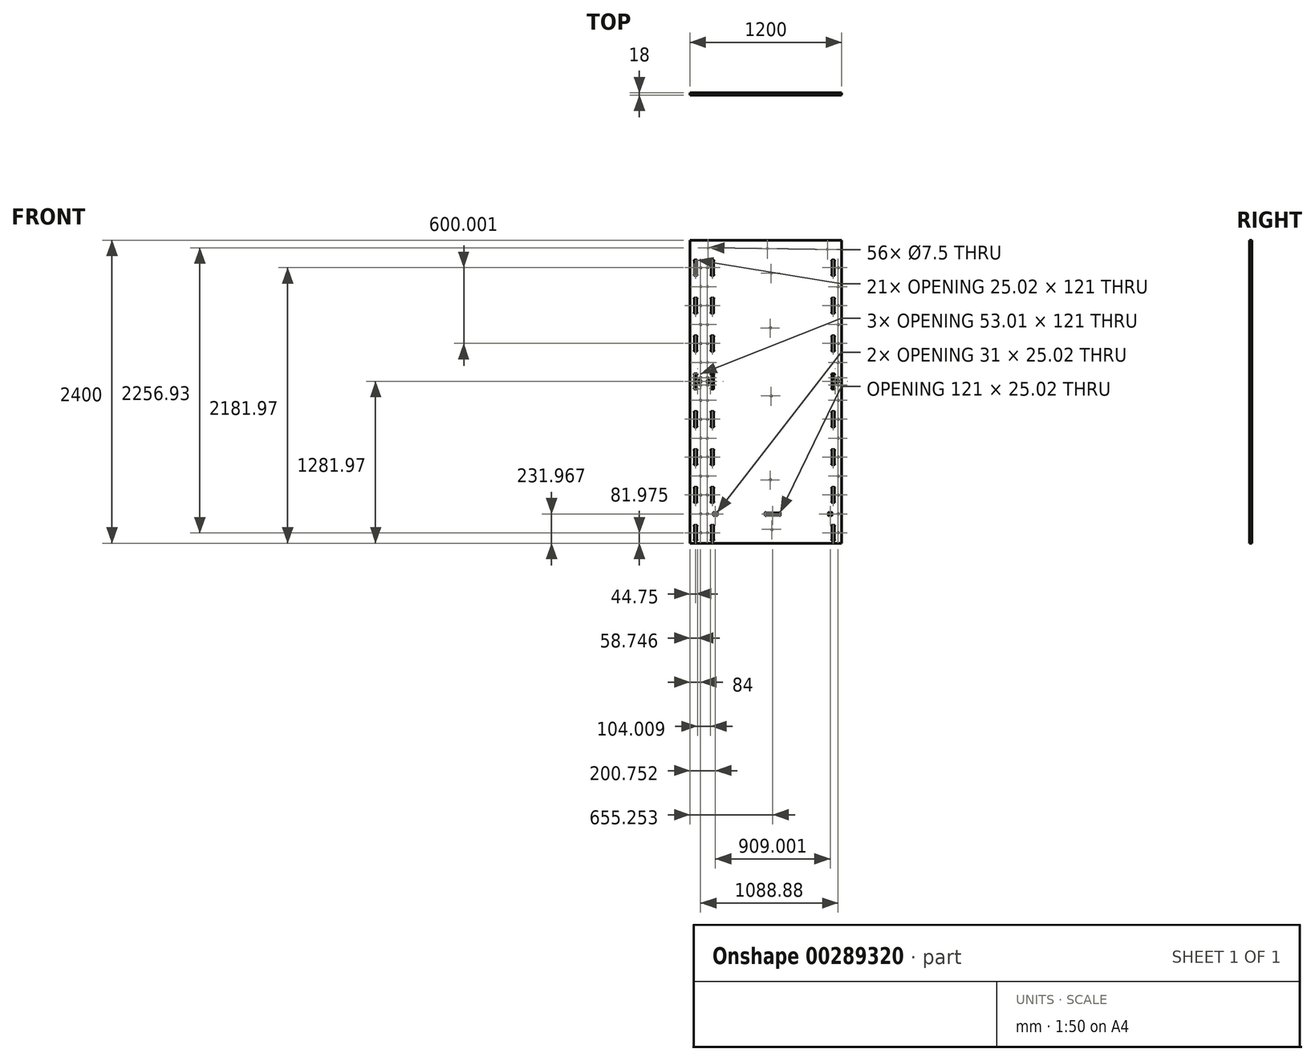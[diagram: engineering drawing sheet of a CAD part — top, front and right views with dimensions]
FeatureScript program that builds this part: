
annotation { "Feature Type Name" : "Feature", "Feature Type Description" : "" }
export const myFeature = defineFeature(function(context is Context, id is Id, definition is map)
    precondition{}
    {
        {
            var Q0;
            Q0=qCreatedBy(makeId("Front.planeOp"),FACE);
            var sketch = newSketch(context, id + "F0", { "sketchPlane" : qUnion([Q0])});
            skLineSegment(sketch, "E0", {"start": v(-600, -1200) * mm, "end": v(600, -1200) * mm});
            skLineSegment(sketch, "E1", {"start": v(600, -1200) * mm, "end": v(600, 1200) * mm});
            skLineSegment(sketch, "E2", {"start": v(600, 1200) * mm, "end": v(-600, 1200) * mm});
            skLineSegment(sketch, "E3", {"start": v(-600, 1200) * mm, "end": v(-600, -1200) * mm});
            skLineSegment(sketch, "E4", {"start": v(-600, 1063.95) * mm, "end": v(-5, 1063.95) * mm});
            skLineSegment(sketch, "E5", {"start": v(-5, 1063.95) * mm, "end": v(-5, 1053.8) * mm});
            skArc(sketch, "E6", {"start": v(-5, 1053.8) * mm, "mid": v(-1.86, 1050.55) * mm, "end": v(1.52, 1053.56) * mm});
            skLineSegment(sketch, "E7", {"start": v(1.52, 1053.56) * mm, "end": v(108.98, 1053.56) * mm});
            skArc(sketch, "E8", {"start": v(108.98, 1053.56) * mm, "mid": v(112.36, 1050.54) * mm, "end": v(115.5, 1053.8) * mm});
            skLineSegment(sketch, "E9", {"start": v(115.5, 1053.8) * mm, "end": v(115.5, 1063.95) * mm});
            skLineSegment(sketch, "E10", {"start": v(115.5, 1063.95) * mm, "end": v(599.5, 1063.95) * mm});
            skLineSegment(sketch, "E11", {"start": v(599.5, 1063.95) * mm, "end": v(599.5, -1200) * mm});
            skArc(sketch, "E12", {"start": v(543, -278.53) * mm, "mid": v(546.26, -275.4) * mm, "end": v(543.25, -272.02) * mm});
            skLineSegment(sketch, "E13", {"start": v(543.25, -272.02) * mm, "end": v(543.25, -164.04) * mm});
            skArc(sketch, "E14", {"start": v(543.25, -164.04) * mm, "mid": v(546.26, -160.67) * mm, "end": v(543, -157.53) * mm});
            skLineSegment(sketch, "E15", {"start": v(543, -157.53) * mm, "end": v(524.5, -157.53) * mm});
            skArc(sketch, "E16", {"start": v(524.5, -157.53) * mm, "mid": v(521.24, -160.67) * mm, "end": v(524.25, -164.04) * mm});
            skLineSegment(sketch, "E17", {"start": v(524.25, -164.04) * mm, "end": v(524.25, -272.02) * mm});
            skArc(sketch, "E18", {"start": v(524.25, -272.02) * mm, "mid": v(521.24, -275.4) * mm, "end": v(524.5, -278.53) * mm});
            skLineSegment(sketch, "E19", {"start": v(524.5, -278.53) * mm, "end": v(543, -278.53) * mm});
            skArc(sketch, "E20", {"start": v(524.25, 27.98) * mm, "mid": v(521.24, 24.6) * mm, "end": v(524.5, 21.47) * mm});
            skLineSegment(sketch, "E21", {"start": v(524.5, 21.47) * mm, "end": v(543, 21.47) * mm});
            skArc(sketch, "E22", {"start": v(543, 21.47) * mm, "mid": v(546.26, 24.6) * mm, "end": v(543.25, 27.98) * mm});
            skLineSegment(sketch, "E23", {"start": v(543.25, 27.98) * mm, "end": v(543.25, 72.47) * mm});
            skLineSegment(sketch, "E24", {"start": v(543.25, 72.47) * mm, "end": v(567.74, 72.47) * mm});
            skArc(sketch, "E25", {"start": v(567.74, 72.47) * mm, "mid": v(571.12, 69.46) * mm, "end": v(574.25, 72.72) * mm});
            skLineSegment(sketch, "E26", {"start": v(574.25, 72.72) * mm, "end": v(574.25, 91.22) * mm});
            skArc(sketch, "E27", {"start": v(574.25, 91.22) * mm, "mid": v(571.12, 94.48) * mm, "end": v(567.74, 91.47) * mm});
            skLineSegment(sketch, "E28", {"start": v(567.74, 91.47) * mm, "end": v(543.25, 91.47) * mm});
            skLineSegment(sketch, "E29", {"start": v(543.25, 91.47) * mm, "end": v(543.25, 135.96) * mm});
            skArc(sketch, "E30", {"start": v(543.25, 135.96) * mm, "mid": v(546.26, 139.33) * mm, "end": v(543, 142.47) * mm});
            skLineSegment(sketch, "E31", {"start": v(543, 142.47) * mm, "end": v(524.5, 142.47) * mm});
            skArc(sketch, "E32", {"start": v(524.5, 142.47) * mm, "mid": v(521.24, 139.33) * mm, "end": v(524.25, 135.96) * mm});
            skLineSegment(sketch, "E33", {"start": v(524.25, 135.96) * mm, "end": v(524.25, 27.98) * mm});
            skArc(sketch, "E34", {"start": v(524.25, 327.98) * mm, "mid": v(521.24, 324.6) * mm, "end": v(524.5, 321.47) * mm});
            skLineSegment(sketch, "E35", {"start": v(524.5, 321.47) * mm, "end": v(543, 321.47) * mm});
            skArc(sketch, "E36", {"start": v(543, 321.47) * mm, "mid": v(546.26, 324.6) * mm, "end": v(543.25, 327.98) * mm});
            skLineSegment(sketch, "E37", {"start": v(543.25, 327.98) * mm, "end": v(543.25, 435.96) * mm});
            skArc(sketch, "E38", {"start": v(543.25, 435.96) * mm, "mid": v(546.26, 439.33) * mm, "end": v(543, 442.47) * mm});
            skLineSegment(sketch, "E39", {"start": v(543, 442.47) * mm, "end": v(524.5, 442.47) * mm});
            skArc(sketch, "E40", {"start": v(524.5, 442.47) * mm, "mid": v(521.24, 439.33) * mm, "end": v(524.25, 435.96) * mm});
            skLineSegment(sketch, "E41", {"start": v(524.25, 435.96) * mm, "end": v(524.25, 327.98) * mm});
            skArc(sketch, "E42", {"start": v(-414, 621.47) * mm, "mid": v(-410.74, 624.6) * mm, "end": v(-413.75, 627.99) * mm});
            skLineSegment(sketch, "E43", {"start": v(-413.75, 627.99) * mm, "end": v(-413.75, 735.96) * mm});
            skArc(sketch, "E44", {"start": v(-413.75, 735.96) * mm, "mid": v(-410.74, 739.34) * mm, "end": v(-414, 742.47) * mm});
            skLineSegment(sketch, "E45", {"start": v(-414, 742.47) * mm, "end": v(-432.5, 742.47) * mm});
            skArc(sketch, "E46", {"start": v(-432.5, 742.47) * mm, "mid": v(-435.76, 739.34) * mm, "end": v(-432.75, 735.96) * mm});
            skLineSegment(sketch, "E47", {"start": v(-432.75, 735.96) * mm, "end": v(-432.75, 627.99) * mm});
            skArc(sketch, "E48", {"start": v(-432.75, 627.99) * mm, "mid": v(-435.76, 624.6) * mm, "end": v(-432.5, 621.47) * mm});
            skLineSegment(sketch, "E49", {"start": v(-432.5, 621.47) * mm, "end": v(-414, 621.47) * mm});
            skArc(sketch, "E50", {"start": v(-432.5, 442.47) * mm, "mid": v(-435.76, 439.34) * mm, "end": v(-432.75, 435.96) * mm});
            skLineSegment(sketch, "E51", {"start": v(-432.75, 435.96) * mm, "end": v(-432.75, 327.99) * mm});
            skArc(sketch, "E52", {"start": v(-432.75, 327.99) * mm, "mid": v(-435.76, 324.6) * mm, "end": v(-432.5, 321.47) * mm});
            skLineSegment(sketch, "E53", {"start": v(-432.5, 321.47) * mm, "end": v(-414, 321.47) * mm});
            skArc(sketch, "E54", {"start": v(-414, 321.47) * mm, "mid": v(-410.74, 324.6) * mm, "end": v(-413.75, 327.99) * mm});
            skLineSegment(sketch, "E55", {"start": v(-413.75, 327.99) * mm, "end": v(-413.75, 435.96) * mm});
            skArc(sketch, "E56", {"start": v(-413.75, 435.96) * mm, "mid": v(-410.74, 439.34) * mm, "end": v(-414, 442.47) * mm});
            skLineSegment(sketch, "E57", {"start": v(-414, 442.47) * mm, "end": v(-432.5, 442.47) * mm});
            skArc(sketch, "E58", {"start": v(-432.5, 142.47) * mm, "mid": v(-435.76, 139.33) * mm, "end": v(-432.75, 135.96) * mm});
            skLineSegment(sketch, "E59", {"start": v(-432.75, 135.96) * mm, "end": v(-432.75, 91.47) * mm});
            skLineSegment(sketch, "E60", {"start": v(-432.75, 91.47) * mm, "end": v(-457.24, 91.47) * mm});
            skArc(sketch, "E61", {"start": v(-457.24, 91.47) * mm, "mid": v(-460.61, 94.47) * mm, "end": v(-463.75, 91.22) * mm});
            skLineSegment(sketch, "E62", {"start": v(-463.75, 91.22) * mm, "end": v(-463.75, 72.72) * mm});
            skArc(sketch, "E63", {"start": v(-463.75, 72.72) * mm, "mid": v(-460.61, 69.46) * mm, "end": v(-457.24, 72.47) * mm});
            skLineSegment(sketch, "E64", {"start": v(-457.24, 72.47) * mm, "end": v(-432.75, 72.47) * mm});
            skLineSegment(sketch, "E65", {"start": v(-432.75, 72.47) * mm, "end": v(-432.75, 27.98) * mm});
            skArc(sketch, "E66", {"start": v(-432.75, 27.98) * mm, "mid": v(-435.76, 24.6) * mm, "end": v(-432.5, 21.47) * mm});
            skLineSegment(sketch, "E67", {"start": v(-432.5, 21.47) * mm, "end": v(-414, 21.47) * mm});
            skArc(sketch, "E68", {"start": v(-414, 21.47) * mm, "mid": v(-410.74, 24.6) * mm, "end": v(-413.75, 27.98) * mm});
            skLineSegment(sketch, "E69", {"start": v(-413.75, 27.98) * mm, "end": v(-413.75, 135.96) * mm});
            skArc(sketch, "E70", {"start": v(-413.75, 135.96) * mm, "mid": v(-410.74, 139.33) * mm, "end": v(-414, 142.47) * mm});
            skLineSegment(sketch, "E71", {"start": v(-414, 142.47) * mm, "end": v(-432.5, 142.47) * mm});
            skArc(sketch, "E72", {"start": v(-432.5, -157.53) * mm, "mid": v(-435.76, -160.66) * mm, "end": v(-432.75, -164.04) * mm});
            skLineSegment(sketch, "E73", {"start": v(-432.75, -164.04) * mm, "end": v(-432.75, -272.02) * mm});
            skArc(sketch, "E74", {"start": v(-432.75, -272.02) * mm, "mid": v(-435.76, -275.4) * mm, "end": v(-432.5, -278.53) * mm});
            skLineSegment(sketch, "E75", {"start": v(-432.5, -278.53) * mm, "end": v(-414, -278.53) * mm});
            skArc(sketch, "E76", {"start": v(-414, -278.53) * mm, "mid": v(-410.74, -275.4) * mm, "end": v(-413.75, -272.02) * mm});
            skLineSegment(sketch, "E77", {"start": v(-413.75, -272.02) * mm, "end": v(-413.75, -164.04) * mm});
            skArc(sketch, "E78", {"start": v(-413.75, -164.04) * mm, "mid": v(-410.74, -160.66) * mm, "end": v(-414, -157.53) * mm});
            skLineSegment(sketch, "E79", {"start": v(-414, -157.53) * mm, "end": v(-432.5, -157.53) * mm});
            skArc(sketch, "E80", {"start": v(-432.5, -457.53) * mm, "mid": v(-435.76, -460.66) * mm, "end": v(-432.75, -464.04) * mm});
            skLineSegment(sketch, "E81", {"start": v(-432.75, -464.04) * mm, "end": v(-432.75, -572.02) * mm});
            skArc(sketch, "E82", {"start": v(-432.75, -572.02) * mm, "mid": v(-435.76, -575.4) * mm, "end": v(-432.5, -578.53) * mm});
            skLineSegment(sketch, "E83", {"start": v(-432.5, -578.53) * mm, "end": v(-414, -578.53) * mm});
            skArc(sketch, "E84", {"start": v(-414, -578.53) * mm, "mid": v(-410.74, -575.4) * mm, "end": v(-413.75, -572.02) * mm});
            skLineSegment(sketch, "E85", {"start": v(-413.75, -572.02) * mm, "end": v(-413.75, -464.04) * mm});
            skArc(sketch, "E86", {"start": v(-413.75, -464.04) * mm, "mid": v(-410.74, -460.66) * mm, "end": v(-414, -457.53) * mm});
            skLineSegment(sketch, "E87", {"start": v(-414, -457.53) * mm, "end": v(-432.5, -457.53) * mm});
            skArc(sketch, "E88", {"start": v(-432.5, -757.53) * mm, "mid": v(-435.76, -760.66) * mm, "end": v(-432.75, -764.04) * mm});
            skLineSegment(sketch, "E89", {"start": v(-432.75, -764.04) * mm, "end": v(-432.75, -872.02) * mm});
            skArc(sketch, "E90", {"start": v(-432.75, -872.02) * mm, "mid": v(-435.76, -875.4) * mm, "end": v(-432.5, -878.53) * mm});
            skLineSegment(sketch, "E91", {"start": v(-432.5, -878.53) * mm, "end": v(-414, -878.53) * mm});
            skArc(sketch, "E92", {"start": v(-414, -878.53) * mm, "mid": v(-410.74, -875.4) * mm, "end": v(-413.75, -872.02) * mm});
            skLineSegment(sketch, "E93", {"start": v(-413.75, -872.02) * mm, "end": v(-413.75, -764.04) * mm});
            skArc(sketch, "E94", {"start": v(-413.75, -764.04) * mm, "mid": v(-410.74, -760.66) * mm, "end": v(-414, -757.53) * mm});
            skLineSegment(sketch, "E95", {"start": v(-414, -757.53) * mm, "end": v(-432.5, -757.53) * mm});
            skArc(sketch, "E96", {"start": v(-545.75, -764.04) * mm, "mid": v(-542.74, -760.66) * mm, "end": v(-546, -757.53) * mm});
            skLineSegment(sketch, "E97", {"start": v(-546, -757.53) * mm, "end": v(-564.5, -757.53) * mm});
            skArc(sketch, "E98", {"start": v(-564.5, -757.53) * mm, "mid": v(-567.76, -760.66) * mm, "end": v(-564.75, -764.04) * mm});
            skLineSegment(sketch, "E99", {"start": v(-564.75, -764.04) * mm, "end": v(-564.75, -872.02) * mm});
            skArc(sketch, "E100", {"start": v(-564.75, -872.02) * mm, "mid": v(-567.76, -875.4) * mm, "end": v(-564.5, -878.53) * mm});
            skLineSegment(sketch, "E101", {"start": v(-564.5, -878.53) * mm, "end": v(-546, -878.53) * mm});
            skArc(sketch, "E102", {"start": v(-546, -878.53) * mm, "mid": v(-542.74, -875.4) * mm, "end": v(-545.75, -872.02) * mm});
            skLineSegment(sketch, "E103", {"start": v(-545.75, -872.02) * mm, "end": v(-545.75, -764.04) * mm});
            skArc(sketch, "E104", {"start": v(-408.24, -958.53) * mm, "mid": v(-411.61, -955.52) * mm, "end": v(-414.75, -958.78) * mm});
            skLineSegment(sketch, "E105", {"start": v(-414.75, -958.78) * mm, "end": v(-414.75, -977.28) * mm});
            skArc(sketch, "E106", {"start": v(-414.75, -977.28) * mm, "mid": v(-411.61, -980.54) * mm, "end": v(-408.24, -977.53) * mm});
            skLineSegment(sketch, "E107", {"start": v(-408.24, -977.53) * mm, "end": v(-390.26, -977.53) * mm});
            skArc(sketch, "E108", {"start": v(-390.26, -977.53) * mm, "mid": v(-386.88, -980.54) * mm, "end": v(-383.75, -977.28) * mm});
            skLineSegment(sketch, "E109", {"start": v(-383.75, -977.28) * mm, "end": v(-383.75, -958.78) * mm});
            skArc(sketch, "E110", {"start": v(-383.75, -958.78) * mm, "mid": v(-386.88, -955.52) * mm, "end": v(-390.26, -958.53) * mm});
            skLineSegment(sketch, "E111", {"start": v(-390.26, -958.53) * mm, "end": v(-408.24, -958.53) * mm});
            skArc(sketch, "E112", {"start": v(-5.25, -977.28) * mm, "mid": v(-2.11, -980.54) * mm, "end": v(1.26, -977.53) * mm});
            skLineSegment(sketch, "E113", {"start": v(1.26, -977.53) * mm, "end": v(109.24, -977.53) * mm});
            skArc(sketch, "E114", {"start": v(109.24, -977.53) * mm, "mid": v(112.62, -980.54) * mm, "end": v(115.75, -977.28) * mm});
            skLineSegment(sketch, "E115", {"start": v(115.75, -977.28) * mm, "end": v(115.75, -958.78) * mm});
            skArc(sketch, "E116", {"start": v(115.75, -958.78) * mm, "mid": v(112.62, -955.52) * mm, "end": v(109.24, -958.53) * mm});
            skLineSegment(sketch, "E117", {"start": v(109.24, -958.53) * mm, "end": v(1.26, -958.53) * mm});
            skArc(sketch, "E118", {"start": v(1.26, -958.53) * mm, "mid": v(-2.11, -955.52) * mm, "end": v(-5.25, -958.78) * mm});
            skLineSegment(sketch, "E119", {"start": v(-5.25, -958.78) * mm, "end": v(-5.25, -977.28) * mm});
            skArc(sketch, "E120", {"start": v(494.25, -977.28) * mm, "mid": v(497.39, -980.54) * mm, "end": v(500.76, -977.53) * mm});
            skLineSegment(sketch, "E121", {"start": v(500.76, -977.53) * mm, "end": v(518.74, -977.53) * mm});
            skArc(sketch, "E122", {"start": v(518.74, -977.53) * mm, "mid": v(522.12, -980.54) * mm, "end": v(525.25, -977.28) * mm});
            skLineSegment(sketch, "E123", {"start": v(525.25, -977.28) * mm, "end": v(525.25, -958.78) * mm});
            skArc(sketch, "E124", {"start": v(525.25, -958.78) * mm, "mid": v(522.12, -955.52) * mm, "end": v(518.74, -958.53) * mm});
            skLineSegment(sketch, "E125", {"start": v(518.74, -958.53) * mm, "end": v(500.76, -958.53) * mm});
            skArc(sketch, "E126", {"start": v(500.76, -958.53) * mm, "mid": v(497.39, -955.52) * mm, "end": v(494.25, -958.78) * mm});
            skLineSegment(sketch, "E127", {"start": v(494.25, -958.78) * mm, "end": v(494.25, -977.28) * mm});
            skArc(sketch, "E128", {"start": v(543, -878.53) * mm, "mid": v(546.26, -875.4) * mm, "end": v(543.25, -872.02) * mm});
            skLineSegment(sketch, "E129", {"start": v(543.25, -872.02) * mm, "end": v(543.25, -764.04) * mm});
            skArc(sketch, "E130", {"start": v(543.25, -764.04) * mm, "mid": v(546.26, -760.67) * mm, "end": v(543, -757.53) * mm});
            skLineSegment(sketch, "E131", {"start": v(543, -757.53) * mm, "end": v(524.5, -757.53) * mm});
            skArc(sketch, "E132", {"start": v(524.5, -757.53) * mm, "mid": v(521.24, -760.67) * mm, "end": v(524.25, -764.04) * mm});
            skLineSegment(sketch, "E133", {"start": v(524.25, -764.04) * mm, "end": v(524.25, -872.02) * mm});
            skArc(sketch, "E134", {"start": v(524.25, -872.02) * mm, "mid": v(521.24, -875.4) * mm, "end": v(524.5, -878.53) * mm});
            skLineSegment(sketch, "E135", {"start": v(524.5, -878.53) * mm, "end": v(543, -878.53) * mm});
            skArc(sketch, "E136", {"start": v(524.25, -572.02) * mm, "mid": v(521.24, -575.4) * mm, "end": v(524.5, -578.53) * mm});
            skLineSegment(sketch, "E137", {"start": v(524.5, -578.53) * mm, "end": v(543, -578.53) * mm});
            skArc(sketch, "E138", {"start": v(543, -578.53) * mm, "mid": v(546.26, -575.4) * mm, "end": v(543.25, -572.02) * mm});
            skLineSegment(sketch, "E139", {"start": v(543.25, -572.02) * mm, "end": v(543.25, -464.04) * mm});
            skArc(sketch, "E140", {"start": v(543.25, -464.04) * mm, "mid": v(546.26, -460.67) * mm, "end": v(543, -457.53) * mm});
            skLineSegment(sketch, "E141", {"start": v(543, -457.53) * mm, "end": v(524.5, -457.53) * mm});
            skArc(sketch, "E142", {"start": v(524.5, -457.53) * mm, "mid": v(521.24, -460.67) * mm, "end": v(524.25, -464.04) * mm});
            skLineSegment(sketch, "E143", {"start": v(524.25, -464.04) * mm, "end": v(524.25, -572.02) * mm});
            skArc(sketch, "E144", {"start": v(524.5, -1057.53) * mm, "mid": v(521.24, -1060.67) * mm, "end": v(524.25, -1064.04) * mm});
            skLineSegment(sketch, "E145", {"start": v(524.25, -1064.04) * mm, "end": v(524.25, -1172.02) * mm});
            skArc(sketch, "E146", {"start": v(524.25, -1172.02) * mm, "mid": v(521.24, -1175.4) * mm, "end": v(524.5, -1178.53) * mm});
            skLineSegment(sketch, "E147", {"start": v(524.5, -1178.53) * mm, "end": v(543, -1178.53) * mm});
            skArc(sketch, "E148", {"start": v(543, -1178.53) * mm, "mid": v(546.26, -1175.4) * mm, "end": v(543.25, -1172.02) * mm});
            skLineSegment(sketch, "E149", {"start": v(543.25, -1172.02) * mm, "end": v(543.25, -1064.04) * mm});
            skArc(sketch, "E150", {"start": v(543.25, -1064.04) * mm, "mid": v(546.26, -1060.67) * mm, "end": v(543, -1057.53) * mm});
            skLineSegment(sketch, "E151", {"start": v(543, -1057.53) * mm, "end": v(524.5, -1057.53) * mm});
            skArc(sketch, "E152", {"start": v(-545.75, -1064.05) * mm, "mid": v(-542.74, -1060.67) * mm, "end": v(-546, -1057.54) * mm});
            skLineSegment(sketch, "E153", {"start": v(-546, -1057.54) * mm, "end": v(-564.5, -1057.54) * mm});
            skArc(sketch, "E154", {"start": v(-564.5, -1057.54) * mm, "mid": v(-567.76, -1060.67) * mm, "end": v(-564.75, -1064.05) * mm});
            skLineSegment(sketch, "E155", {"start": v(-564.75, -1064.05) * mm, "end": v(-564.75, -1172.03) * mm});
            skArc(sketch, "E156", {"start": v(-564.75, -1172.03) * mm, "mid": v(-567.76, -1175.4) * mm, "end": v(-564.5, -1178.54) * mm});
            skLineSegment(sketch, "E157", {"start": v(-564.5, -1178.54) * mm, "end": v(-546, -1178.54) * mm});
            skArc(sketch, "E158", {"start": v(-546, -1178.54) * mm, "mid": v(-542.74, -1175.4) * mm, "end": v(-545.75, -1172.03) * mm});
            skLineSegment(sketch, "E159", {"start": v(-545.75, -1172.03) * mm, "end": v(-545.75, -1064.05) * mm});
            skLineSegment(sketch, "E160", {"start": v(-432.75, -1064.05) * mm, "end": v(-432.75, -1172.03) * mm});
            skArc(sketch, "E161", {"start": v(-432.75, -1172.03) * mm, "mid": v(-435.76, -1175.4) * mm, "end": v(-432.5, -1178.54) * mm});
            skLineSegment(sketch, "E162", {"start": v(-432.5, -1178.54) * mm, "end": v(-414, -1178.54) * mm});
            skArc(sketch, "E163", {"start": v(-414, -1178.54) * mm, "mid": v(-410.74, -1175.4) * mm, "end": v(-413.75, -1172.03) * mm});
            skLineSegment(sketch, "E164", {"start": v(-413.75, -1172.03) * mm, "end": v(-413.75, -1064.05) * mm});
            skArc(sketch, "E165", {"start": v(-413.75, -1064.05) * mm, "mid": v(-410.74, -1060.67) * mm, "end": v(-414, -1057.54) * mm});
            skLineSegment(sketch, "E166", {"start": v(-414, -1057.54) * mm, "end": v(-432.5, -1057.54) * mm});
            skArc(sketch, "E167", {"start": v(-432.5, -1057.54) * mm, "mid": v(-435.76, -1060.67) * mm, "end": v(-432.75, -1064.05) * mm});
            skArc(sketch, "E168", {"start": v(-545.75, -464.04) * mm, "mid": v(-542.74, -460.66) * mm, "end": v(-546, -457.53) * mm});
            skLineSegment(sketch, "E169", {"start": v(-546, -457.53) * mm, "end": v(-564.5, -457.53) * mm});
            skArc(sketch, "E170", {"start": v(-564.5, -457.53) * mm, "mid": v(-567.76, -460.66) * mm, "end": v(-564.75, -464.04) * mm});
            skLineSegment(sketch, "E171", {"start": v(-564.75, -464.04) * mm, "end": v(-564.75, -572.02) * mm});
            skArc(sketch, "E172", {"start": v(-564.75, -572.02) * mm, "mid": v(-567.76, -575.4) * mm, "end": v(-564.5, -578.53) * mm});
            skLineSegment(sketch, "E173", {"start": v(-564.5, -578.53) * mm, "end": v(-546, -578.53) * mm});
            skArc(sketch, "E174", {"start": v(-546, -578.53) * mm, "mid": v(-542.74, -575.4) * mm, "end": v(-545.75, -572.02) * mm});
            skLineSegment(sketch, "E175", {"start": v(-545.75, -572.02) * mm, "end": v(-545.75, -464.04) * mm});
            skArc(sketch, "E176", {"start": v(-545.75, -164.04) * mm, "mid": v(-542.74, -160.66) * mm, "end": v(-546, -157.53) * mm});
            skLineSegment(sketch, "E177", {"start": v(-546, -157.53) * mm, "end": v(-564.5, -157.53) * mm});
            skArc(sketch, "E178", {"start": v(-564.5, -157.53) * mm, "mid": v(-567.76, -160.66) * mm, "end": v(-564.75, -164.04) * mm});
            skLineSegment(sketch, "E179", {"start": v(-564.75, -164.04) * mm, "end": v(-564.75, -272.02) * mm});
            skArc(sketch, "E180", {"start": v(-564.75, -272.02) * mm, "mid": v(-567.76, -275.4) * mm, "end": v(-564.5, -278.53) * mm});
            skLineSegment(sketch, "E181", {"start": v(-564.5, -278.53) * mm, "end": v(-546, -278.53) * mm});
            skArc(sketch, "E182", {"start": v(-546, -278.53) * mm, "mid": v(-542.74, -275.4) * mm, "end": v(-545.75, -272.02) * mm});
            skLineSegment(sketch, "E183", {"start": v(-545.75, -272.02) * mm, "end": v(-545.75, -164.04) * mm});
            skArc(sketch, "E184", {"start": v(-545.75, 135.96) * mm, "mid": v(-542.74, 139.33) * mm, "end": v(-546, 142.47) * mm});
            skLineSegment(sketch, "E185", {"start": v(-546, 142.47) * mm, "end": v(-564.5, 142.47) * mm});
            skArc(sketch, "E186", {"start": v(-564.5, 142.47) * mm, "mid": v(-567.76, 139.33) * mm, "end": v(-564.75, 135.96) * mm});
            skLineSegment(sketch, "E187", {"start": v(-564.75, 135.96) * mm, "end": v(-564.75, 27.98) * mm});
            skArc(sketch, "E188", {"start": v(-564.75, 27.98) * mm, "mid": v(-567.76, 24.6) * mm, "end": v(-564.5, 21.47) * mm});
            skLineSegment(sketch, "E189", {"start": v(-564.5, 21.47) * mm, "end": v(-546, 21.47) * mm});
            skArc(sketch, "E190", {"start": v(-546, 21.47) * mm, "mid": v(-542.74, 24.6) * mm, "end": v(-545.75, 27.98) * mm});
            skLineSegment(sketch, "E191", {"start": v(-545.75, 27.98) * mm, "end": v(-545.75, 72.47) * mm});
            skLineSegment(sketch, "E192", {"start": v(-545.75, 72.47) * mm, "end": v(-521.26, 72.47) * mm});
            skArc(sketch, "E193", {"start": v(-521.26, 72.47) * mm, "mid": v(-517.89, 69.46) * mm, "end": v(-514.75, 72.72) * mm});
            skLineSegment(sketch, "E194", {"start": v(-514.75, 72.72) * mm, "end": v(-514.75, 91.22) * mm});
            skArc(sketch, "E195", {"start": v(-514.75, 91.22) * mm, "mid": v(-517.89, 94.48) * mm, "end": v(-521.26, 91.47) * mm});
            skLineSegment(sketch, "E196", {"start": v(-521.26, 91.47) * mm, "end": v(-545.75, 91.47) * mm});
            skLineSegment(sketch, "E197", {"start": v(-545.75, 91.47) * mm, "end": v(-545.75, 135.96) * mm});
            skArc(sketch, "E198", {"start": v(-545.75, 435.96) * mm, "mid": v(-542.74, 439.34) * mm, "end": v(-546, 442.47) * mm});
            skLineSegment(sketch, "E199", {"start": v(-546, 442.47) * mm, "end": v(-564.5, 442.47) * mm});
            skArc(sketch, "E200", {"start": v(-564.5, 442.47) * mm, "mid": v(-567.76, 439.34) * mm, "end": v(-564.75, 435.96) * mm});
            skLineSegment(sketch, "E201", {"start": v(-564.75, 435.96) * mm, "end": v(-564.75, 327.98) * mm});
            skArc(sketch, "E202", {"start": v(-564.75, 327.98) * mm, "mid": v(-567.76, 324.6) * mm, "end": v(-564.5, 321.47) * mm});
            skLineSegment(sketch, "E203", {"start": v(-564.5, 321.47) * mm, "end": v(-546, 321.47) * mm});
            skArc(sketch, "E204", {"start": v(-546, 321.47) * mm, "mid": v(-542.74, 324.6) * mm, "end": v(-545.75, 327.98) * mm});
            skLineSegment(sketch, "E205", {"start": v(-545.75, 327.98) * mm, "end": v(-545.75, 435.96) * mm});
            skArc(sketch, "E206", {"start": v(-545.75, 735.96) * mm, "mid": v(-542.74, 739.34) * mm, "end": v(-546, 742.47) * mm});
            skLineSegment(sketch, "E207", {"start": v(-546, 742.47) * mm, "end": v(-564.5, 742.47) * mm});
            skArc(sketch, "E208", {"start": v(-564.5, 742.47) * mm, "mid": v(-567.76, 739.34) * mm, "end": v(-564.75, 735.96) * mm});
            skLineSegment(sketch, "E209", {"start": v(-564.75, 735.96) * mm, "end": v(-564.75, 627.99) * mm});
            skArc(sketch, "E210", {"start": v(-564.75, 627.99) * mm, "mid": v(-567.76, 624.6) * mm, "end": v(-564.5, 621.47) * mm});
            skLineSegment(sketch, "E211", {"start": v(-564.5, 621.47) * mm, "end": v(-546, 621.47) * mm});
            skArc(sketch, "E212", {"start": v(-546, 621.47) * mm, "mid": v(-542.74, 624.6) * mm, "end": v(-545.75, 627.99) * mm});
            skLineSegment(sketch, "E213", {"start": v(-545.75, 627.99) * mm, "end": v(-545.75, 735.96) * mm});
            skArc(sketch, "E214", {"start": v(-414, 921.47) * mm, "mid": v(-410.74, 924.6) * mm, "end": v(-413.75, 927.99) * mm});
            skLineSegment(sketch, "E215", {"start": v(-413.75, 927.99) * mm, "end": v(-413.75, 1035.96) * mm});
            skArc(sketch, "E216", {"start": v(-413.75, 1035.96) * mm, "mid": v(-410.74, 1039.34) * mm, "end": v(-414, 1042.47) * mm});
            skLineSegment(sketch, "E217", {"start": v(-414, 1042.47) * mm, "end": v(-432.5, 1042.47) * mm});
            skArc(sketch, "E218", {"start": v(-432.5, 1042.47) * mm, "mid": v(-435.76, 1039.34) * mm, "end": v(-432.75, 1035.96) * mm});
            skLineSegment(sketch, "E219", {"start": v(-432.75, 1035.96) * mm, "end": v(-432.75, 927.99) * mm});
            skArc(sketch, "E220", {"start": v(-432.75, 927.99) * mm, "mid": v(-435.76, 924.6) * mm, "end": v(-432.5, 921.47) * mm});
            skLineSegment(sketch, "E221", {"start": v(-432.5, 921.47) * mm, "end": v(-414, 921.47) * mm});
            skLineSegment(sketch, "E222", {"start": v(-545.75, 927.99) * mm, "end": v(-545.75, 1035.96) * mm});
            skArc(sketch, "E223", {"start": v(-545.75, 1035.96) * mm, "mid": v(-542.74, 1039.34) * mm, "end": v(-546, 1042.47) * mm});
            skLineSegment(sketch, "E224", {"start": v(-546, 1042.47) * mm, "end": v(-564.5, 1042.47) * mm});
            skArc(sketch, "E225", {"start": v(-564.5, 1042.47) * mm, "mid": v(-567.76, 1039.34) * mm, "end": v(-564.75, 1035.96) * mm});
            skLineSegment(sketch, "E226", {"start": v(-564.75, 1035.96) * mm, "end": v(-564.75, 927.99) * mm});
            skArc(sketch, "E227", {"start": v(-564.75, 927.99) * mm, "mid": v(-567.76, 924.6) * mm, "end": v(-564.5, 921.47) * mm});
            skLineSegment(sketch, "E228", {"start": v(-564.5, 921.47) * mm, "end": v(-546, 921.47) * mm});
            skArc(sketch, "E229", {"start": v(-546, 921.47) * mm, "mid": v(-542.74, 924.6) * mm, "end": v(-545.75, 927.99) * mm});
            skArc(sketch, "E230", {"start": v(524.25, 627.98) * mm, "mid": v(521.24, 624.6) * mm, "end": v(524.5, 621.47) * mm});
            skLineSegment(sketch, "E231", {"start": v(524.5, 621.47) * mm, "end": v(543, 621.47) * mm});
            skArc(sketch, "E232", {"start": v(543, 621.47) * mm, "mid": v(546.26, 624.6) * mm, "end": v(543.25, 627.98) * mm});
            skLineSegment(sketch, "E233", {"start": v(543.25, 627.98) * mm, "end": v(543.25, 735.96) * mm});
            skArc(sketch, "E234", {"start": v(543.25, 735.96) * mm, "mid": v(546.26, 739.33) * mm, "end": v(543, 742.47) * mm});
            skLineSegment(sketch, "E235", {"start": v(543, 742.47) * mm, "end": v(524.5, 742.47) * mm});
            skArc(sketch, "E236", {"start": v(524.5, 742.47) * mm, "mid": v(521.24, 739.33) * mm, "end": v(524.25, 735.96) * mm});
            skLineSegment(sketch, "E237", {"start": v(524.25, 735.96) * mm, "end": v(524.25, 627.98) * mm});
            skArc(sketch, "E238", {"start": v(524.25, 927.98) * mm, "mid": v(521.24, 924.6) * mm, "end": v(524.5, 921.47) * mm});
            skLineSegment(sketch, "E239", {"start": v(524.5, 921.47) * mm, "end": v(543, 921.47) * mm});
            skArc(sketch, "E240", {"start": v(543, 921.47) * mm, "mid": v(546.26, 924.6) * mm, "end": v(543.25, 927.98) * mm});
            skLineSegment(sketch, "E241", {"start": v(543.25, 927.98) * mm, "end": v(543.25, 1035.96) * mm});
            skArc(sketch, "E242", {"start": v(543.25, 1035.96) * mm, "mid": v(546.26, 1039.33) * mm, "end": v(543, 1042.47) * mm});
            skLineSegment(sketch, "E243", {"start": v(543, 1042.47) * mm, "end": v(524.5, 1042.47) * mm});
            skArc(sketch, "E244", {"start": v(524.5, 1042.47) * mm, "mid": v(521.24, 1039.33) * mm, "end": v(524.25, 1035.96) * mm});
            skLineSegment(sketch, "E245", {"start": v(524.25, 1035.96) * mm, "end": v(524.25, 927.98) * mm});
            skLineSegment(sketch, "E246", {"start": v(-49.83, 116.75) * mm, "end": v(-49.83, 156.7) * mm});
            skLineSegment(sketch, "E247", {"start": v(-49.83, 156.7) * mm, "end": v(-32.27, 156.7) * mm});
            skLineSegment(sketch, "E248", {"start": v(-32.27, 156.7) * mm, "end": v(-31.78, 156.7) * mm});
            skLineSegment(sketch, "E249", {"start": v(-31.78, 156.7) * mm, "end": v(-31.29, 156.67) * mm});
            skLineSegment(sketch, "E250", {"start": v(-31.29, 156.67) * mm, "end": v(-30.8, 156.62) * mm});
            skLineSegment(sketch, "E251", {"start": v(-30.8, 156.62) * mm, "end": v(-30.32, 156.54) * mm});
            skLineSegment(sketch, "E252", {"start": v(-30.32, 156.54) * mm, "end": v(-29.84, 156.44) * mm});
            skLineSegment(sketch, "E253", {"start": v(-29.84, 156.44) * mm, "end": v(-29.37, 156.3) * mm});
            skLineSegment(sketch, "E254", {"start": v(-29.37, 156.3) * mm, "end": v(-28.9, 156.16) * mm});
            skLineSegment(sketch, "E255", {"start": v(-28.9, 156.16) * mm, "end": v(-28.45, 155.98) * mm});
            skLineSegment(sketch, "E256", {"start": v(-28.45, 155.98) * mm, "end": v(-28, 155.79) * mm});
            skLineSegment(sketch, "E257", {"start": v(-28, 155.79) * mm, "end": v(-27.57, 155.57) * mm});
            skLineSegment(sketch, "E258", {"start": v(-27.57, 155.57) * mm, "end": v(-27.15, 155.33) * mm});
            skLineSegment(sketch, "E259", {"start": v(-27.15, 155.33) * mm, "end": v(-26.74, 155.06) * mm});
            skLineSegment(sketch, "E260", {"start": v(-26.74, 155.06) * mm, "end": v(-26.34, 154.78) * mm});
            skLineSegment(sketch, "E261", {"start": v(-26.34, 154.78) * mm, "end": v(-25.95, 154.47) * mm});
            skLineSegment(sketch, "E262", {"start": v(-25.95, 154.47) * mm, "end": v(-25.58, 154.15) * mm});
            skLineSegment(sketch, "E263", {"start": v(-25.58, 154.15) * mm, "end": v(-25.23, 153.8) * mm});
            skLineSegment(sketch, "E264", {"start": v(-25.23, 153.8) * mm, "end": v(-24.9, 153.45) * mm});
            skLineSegment(sketch, "E265", {"start": v(-24.9, 153.45) * mm, "end": v(-24.57, 153.09) * mm});
            skLineSegment(sketch, "E266", {"start": v(-24.57, 153.09) * mm, "end": v(-24.27, 152.7) * mm});
            skLineSegment(sketch, "E267", {"start": v(-24.27, 152.7) * mm, "end": v(-23.99, 152.3) * mm});
            skLineSegment(sketch, "E268", {"start": v(-23.99, 152.3) * mm, "end": v(-23.73, 151.9) * mm});
            skLineSegment(sketch, "E269", {"start": v(-23.73, 151.9) * mm, "end": v(-23.49, 151.48) * mm});
            skLineSegment(sketch, "E270", {"start": v(-23.49, 151.48) * mm, "end": v(-23.27, 151.05) * mm});
            skLineSegment(sketch, "E271", {"start": v(-23.27, 151.05) * mm, "end": v(-23.07, 150.6) * mm});
            skLineSegment(sketch, "E272", {"start": v(-23.07, 150.6) * mm, "end": v(-22.9, 150.16) * mm});
            skLineSegment(sketch, "E273", {"start": v(-22.9, 150.16) * mm, "end": v(-22.74, 149.7) * mm});
            skLineSegment(sketch, "E274", {"start": v(-22.74, 149.7) * mm, "end": v(-22.61, 149.24) * mm});
            skLineSegment(sketch, "E275", {"start": v(-22.61, 149.24) * mm, "end": v(-22.5, 148.76) * mm});
            skLineSegment(sketch, "E276", {"start": v(-22.5, 148.76) * mm, "end": v(-22.42, 148.29) * mm});
            skLineSegment(sketch, "E277", {"start": v(-22.42, 148.29) * mm, "end": v(-22.36, 147.8) * mm});
            skLineSegment(sketch, "E278", {"start": v(-22.36, 147.8) * mm, "end": v(-22.33, 147.32) * mm});
            skLineSegment(sketch, "E279", {"start": v(-22.33, 147.32) * mm, "end": v(-22.31, 146.83) * mm});
            skLineSegment(sketch, "E280", {"start": v(-22.31, 146.83) * mm, "end": v(-22.31, 146.33) * mm});
            skLineSegment(sketch, "E281", {"start": v(-22.31, 146.33) * mm, "end": v(-22.33, 145.83) * mm});
            skLineSegment(sketch, "E282", {"start": v(-22.33, 145.83) * mm, "end": v(-22.38, 145.33) * mm});
            skLineSegment(sketch, "E283", {"start": v(-22.38, 145.33) * mm, "end": v(-22.46, 144.84) * mm});
            skLineSegment(sketch, "E284", {"start": v(-22.46, 144.84) * mm, "end": v(-22.55, 144.35) * mm});
            skLineSegment(sketch, "E285", {"start": v(-22.55, 144.35) * mm, "end": v(-22.68, 143.87) * mm});
            skLineSegment(sketch, "E286", {"start": v(-22.68, 143.87) * mm, "end": v(-22.82, 143.4) * mm});
            skLineSegment(sketch, "E287", {"start": v(-22.82, 143.4) * mm, "end": v(-23, 142.94) * mm});
            skLineSegment(sketch, "E288", {"start": v(-23, 142.94) * mm, "end": v(-23.18, 142.48) * mm});
            skLineSegment(sketch, "E289", {"start": v(-23.18, 142.48) * mm, "end": v(-23.4, 142.04) * mm});
            skLineSegment(sketch, "E290", {"start": v(-23.4, 142.04) * mm, "end": v(-23.64, 141.6) * mm});
            skLineSegment(sketch, "E291", {"start": v(-23.64, 141.6) * mm, "end": v(-23.9, 141.18) * mm});
            skLineSegment(sketch, "E292", {"start": v(-23.9, 141.18) * mm, "end": v(-24.18, 140.77) * mm});
            skLineSegment(sketch, "E293", {"start": v(-24.18, 140.77) * mm, "end": v(-24.48, 140.38) * mm});
            skLineSegment(sketch, "E294", {"start": v(-24.48, 140.38) * mm, "end": v(-24.8, 140) * mm});
            skLineSegment(sketch, "E295", {"start": v(-24.8, 140) * mm, "end": v(-25.15, 139.63) * mm});
            skLineSegment(sketch, "E296", {"start": v(-25.15, 139.63) * mm, "end": v(-25.51, 139.29) * mm});
            skLineSegment(sketch, "E297", {"start": v(-25.51, 139.29) * mm, "end": v(-25.89, 138.96) * mm});
            skLineSegment(sketch, "E298", {"start": v(-25.89, 138.96) * mm, "end": v(-26.28, 138.66) * mm});
            skLineSegment(sketch, "E299", {"start": v(-26.28, 138.66) * mm, "end": v(-26.68, 138.38) * mm});
            skLineSegment(sketch, "E300", {"start": v(-26.68, 138.38) * mm, "end": v(-27.1, 138.12) * mm});
            skLineSegment(sketch, "E301", {"start": v(-27.1, 138.12) * mm, "end": v(-27.53, 137.88) * mm});
            skLineSegment(sketch, "E302", {"start": v(-27.53, 137.88) * mm, "end": v(-27.97, 137.66) * mm});
            skLineSegment(sketch, "E303", {"start": v(-27.97, 137.66) * mm, "end": v(-28.42, 137.46) * mm});
            skLineSegment(sketch, "E304", {"start": v(-28.42, 137.46) * mm, "end": v(-28.88, 137.29) * mm});
            skLineSegment(sketch, "E305", {"start": v(-28.88, 137.29) * mm, "end": v(-29.35, 137.14) * mm});
            skLineSegment(sketch, "E306", {"start": v(-29.35, 137.14) * mm, "end": v(-29.82, 137) * mm});
            skLineSegment(sketch, "E307", {"start": v(-29.82, 137) * mm, "end": v(-30.3, 136.9) * mm});
            skLineSegment(sketch, "E308", {"start": v(-30.3, 136.9) * mm, "end": v(-30.79, 136.83) * mm});
            skLineSegment(sketch, "E309", {"start": v(-30.79, 136.83) * mm, "end": v(-31.28, 136.77) * mm});
            skLineSegment(sketch, "E310", {"start": v(-31.28, 136.77) * mm, "end": v(-31.78, 136.74) * mm});
            skLineSegment(sketch, "E311", {"start": v(-31.78, 136.74) * mm, "end": v(-32.27, 136.73) * mm});
            skLineSegment(sketch, "E312", {"start": v(-32.27, 136.73) * mm, "end": v(-49.83, 136.73) * mm});
            skLineSegment(sketch, "E313", {"start": v(-32.27, 136.73) * mm, "end": v(-31.86, 136.73) * mm});
            skLineSegment(sketch, "E314", {"start": v(-31.86, 136.73) * mm, "end": v(-31.46, 136.7) * mm});
            skLineSegment(sketch, "E315", {"start": v(-31.46, 136.7) * mm, "end": v(-31.05, 136.67) * mm});
            skLineSegment(sketch, "E316", {"start": v(-31.05, 136.67) * mm, "end": v(-30.65, 136.6) * mm});
            skLineSegment(sketch, "E317", {"start": v(-30.65, 136.6) * mm, "end": v(-30.26, 136.52) * mm});
            skLineSegment(sketch, "E318", {"start": v(-30.26, 136.52) * mm, "end": v(-29.87, 136.41) * mm});
            skLineSegment(sketch, "E319", {"start": v(-29.87, 136.41) * mm, "end": v(-29.48, 136.3) * mm});
            skLineSegment(sketch, "E320", {"start": v(-29.48, 136.3) * mm, "end": v(-29.1, 136.15) * mm});
            skLineSegment(sketch, "E321", {"start": v(-29.1, 136.15) * mm, "end": v(-28.73, 135.99) * mm});
            skLineSegment(sketch, "E322", {"start": v(-28.73, 135.99) * mm, "end": v(-28.37, 135.8) * mm});
            skLineSegment(sketch, "E323", {"start": v(-28.37, 135.8) * mm, "end": v(-28.02, 135.6) * mm});
            skLineSegment(sketch, "E324", {"start": v(-28.02, 135.6) * mm, "end": v(-27.68, 135.4) * mm});
            skLineSegment(sketch, "E325", {"start": v(-27.68, 135.4) * mm, "end": v(-27.35, 135.16) * mm});
            skLineSegment(sketch, "E326", {"start": v(-27.35, 135.16) * mm, "end": v(-27.03, 134.9) * mm});
            skLineSegment(sketch, "E327", {"start": v(-27.03, 134.9) * mm, "end": v(-26.72, 134.64) * mm});
            skLineSegment(sketch, "E328", {"start": v(-26.72, 134.64) * mm, "end": v(-26.42, 134.35) * mm});
            skLineSegment(sketch, "E329", {"start": v(-26.42, 134.35) * mm, "end": v(-26.08, 133.85) * mm});
            skLineSegment(sketch, "E330", {"start": v(-26.08, 133.85) * mm, "end": v(-25.76, 133.34) * mm});
            skLineSegment(sketch, "E331", {"start": v(-25.76, 133.34) * mm, "end": v(-25.47, 132.81) * mm});
            skLineSegment(sketch, "E332", {"start": v(-25.47, 132.81) * mm, "end": v(-25.2, 132.28) * mm});
            skLineSegment(sketch, "E333", {"start": v(-25.2, 132.28) * mm, "end": v(-24.96, 131.73) * mm});
            skLineSegment(sketch, "E334", {"start": v(-24.96, 131.73) * mm, "end": v(-24.74, 131.17) * mm});
            skLineSegment(sketch, "E335", {"start": v(-24.74, 131.17) * mm, "end": v(-24.54, 130.6) * mm});
            skLineSegment(sketch, "E336", {"start": v(-24.54, 130.6) * mm, "end": v(-24.37, 130.03) * mm});
            skLineSegment(sketch, "E337", {"start": v(-24.37, 130.03) * mm, "end": v(-24.23, 129.45) * mm});
            skLineSegment(sketch, "E338", {"start": v(-24.23, 129.45) * mm, "end": v(-24.11, 128.86) * mm});
            skLineSegment(sketch, "E339", {"start": v(-24.11, 128.86) * mm, "end": v(-24.02, 128.27) * mm});
            skLineSegment(sketch, "E340", {"start": v(-24.02, 128.27) * mm, "end": v(-23.96, 127.67) * mm});
            skLineSegment(sketch, "E341", {"start": v(-23.96, 127.67) * mm, "end": v(-23.92, 127.07) * mm});
            skLineSegment(sketch, "E342", {"start": v(-23.92, 127.07) * mm, "end": v(-23.9, 126.47) * mm});
            skLineSegment(sketch, "E343", {"start": v(-23.9, 126.47) * mm, "end": v(-23.92, 125.87) * mm});
            skLineSegment(sketch, "E344", {"start": v(-23.92, 125.87) * mm, "end": v(-23.96, 125.27) * mm});
            skLineSegment(sketch, "E345", {"start": v(-23.96, 125.27) * mm, "end": v(-23.97, 124.73) * mm});
            skLineSegment(sketch, "E346", {"start": v(-23.97, 124.73) * mm, "end": v(-23.97, 124.19) * mm});
            skLineSegment(sketch, "E347", {"start": v(-23.97, 124.19) * mm, "end": v(-23.96, 123.65) * mm});
            skLineSegment(sketch, "E348", {"start": v(-23.96, 123.65) * mm, "end": v(-23.94, 123.11) * mm});
            skLineSegment(sketch, "E349", {"start": v(-23.94, 123.11) * mm, "end": v(-23.9, 122.58) * mm});
            skLineSegment(sketch, "E350", {"start": v(-23.9, 122.58) * mm, "end": v(-23.86, 122.04) * mm});
            skLineSegment(sketch, "E351", {"start": v(-23.86, 122.04) * mm, "end": v(-23.81, 121.5) * mm});
            skLineSegment(sketch, "E352", {"start": v(-23.81, 121.5) * mm, "end": v(-23.75, 120.97) * mm});
            skLineSegment(sketch, "E353", {"start": v(-23.75, 120.97) * mm, "end": v(-23.68, 120.43) * mm});
            skLineSegment(sketch, "E354", {"start": v(-23.68, 120.43) * mm, "end": v(-23.6, 119.9) * mm});
            skLineSegment(sketch, "E355", {"start": v(-23.6, 119.9) * mm, "end": v(-23.52, 119.37) * mm});
            skLineSegment(sketch, "E356", {"start": v(-23.52, 119.37) * mm, "end": v(-23.42, 118.84) * mm});
            skLineSegment(sketch, "E357", {"start": v(-23.42, 118.84) * mm, "end": v(-23.31, 118.31) * mm});
            skLineSegment(sketch, "E358", {"start": v(-23.31, 118.31) * mm, "end": v(-23.2, 117.79) * mm});
            skLineSegment(sketch, "E359", {"start": v(-23.2, 117.79) * mm, "end": v(-23.07, 117.27) * mm});
            skLineSegment(sketch, "E360", {"start": v(-23.07, 117.27) * mm, "end": v(-22.93, 116.75) * mm});
            skLineSegment(sketch, "E361", {"start": v(2.97, 116.19) * mm, "end": v(2.55, 116.18) * mm});
            skLineSegment(sketch, "E362", {"start": v(2.55, 116.18) * mm, "end": v(2.14, 116.19) * mm});
            skLineSegment(sketch, "E363", {"start": v(2.14, 116.19) * mm, "end": v(1.72, 116.2) * mm});
            skLineSegment(sketch, "E364", {"start": v(1.72, 116.2) * mm, "end": v(1.3, 116.23) * mm});
            skLineSegment(sketch, "E365", {"start": v(1.3, 116.23) * mm, "end": v(0.89, 116.27) * mm});
            skLineSegment(sketch, "E366", {"start": v(0.89, 116.27) * mm, "end": v(0.47, 116.32) * mm});
            skLineSegment(sketch, "E367", {"start": v(0.47, 116.32) * mm, "end": v(0.06, 116.38) * mm});
            skLineSegment(sketch, "E368", {"start": v(0.06, 116.38) * mm, "end": v(-0.35, 116.45) * mm});
            skLineSegment(sketch, "E369", {"start": v(-0.35, 116.45) * mm, "end": v(-0.76, 116.53) * mm});
            skLineSegment(sketch, "E370", {"start": v(-0.76, 116.53) * mm, "end": v(-1.16, 116.62) * mm});
            skLineSegment(sketch, "E371", {"start": v(-1.16, 116.62) * mm, "end": v(-1.56, 116.72) * mm});
            skLineSegment(sketch, "E372", {"start": v(-1.56, 116.72) * mm, "end": v(-1.96, 116.83) * mm});
            skLineSegment(sketch, "E373", {"start": v(-1.96, 116.83) * mm, "end": v(-2.36, 116.95) * mm});
            skLineSegment(sketch, "E374", {"start": v(-2.36, 116.95) * mm, "end": v(-2.75, 117.08) * mm});
            skLineSegment(sketch, "E375", {"start": v(-2.75, 117.08) * mm, "end": v(-3.14, 117.22) * mm});
            skLineSegment(sketch, "E376", {"start": v(-3.14, 117.22) * mm, "end": v(-3.53, 117.37) * mm});
            skLineSegment(sketch, "E377", {"start": v(-3.53, 117.37) * mm, "end": v(-3.91, 117.52) * mm});
            skLineSegment(sketch, "E378", {"start": v(-3.91, 117.52) * mm, "end": v(-4.29, 117.7) * mm});
            skLineSegment(sketch, "E379", {"start": v(-4.29, 117.7) * mm, "end": v(-4.66, 117.87) * mm});
            skLineSegment(sketch, "E380", {"start": v(-4.66, 117.87) * mm, "end": v(-5.03, 118.05) * mm});
            skLineSegment(sketch, "E381", {"start": v(-5.03, 118.05) * mm, "end": v(-5.4, 118.25) * mm});
            skLineSegment(sketch, "E382", {"start": v(-5.4, 118.25) * mm, "end": v(-5.76, 118.45) * mm});
            skLineSegment(sketch, "E383", {"start": v(-5.76, 118.45) * mm, "end": v(-6.11, 118.67) * mm});
            skLineSegment(sketch, "E384", {"start": v(-6.11, 118.67) * mm, "end": v(-6.47, 118.89) * mm});
            skLineSegment(sketch, "E385", {"start": v(-6.47, 118.89) * mm, "end": v(-6.81, 119.12) * mm});
            skLineSegment(sketch, "E386", {"start": v(-6.81, 119.12) * mm, "end": v(-7.15, 119.36) * mm});
            skLineSegment(sketch, "E387", {"start": v(-7.15, 119.36) * mm, "end": v(-7.48, 119.6) * mm});
            skLineSegment(sketch, "E388", {"start": v(-7.48, 119.6) * mm, "end": v(-7.81, 119.86) * mm});
            skLineSegment(sketch, "E389", {"start": v(-7.81, 119.86) * mm, "end": v(-8.13, 120.13) * mm});
            skLineSegment(sketch, "E390", {"start": v(-8.13, 120.13) * mm, "end": v(-8.45, 120.4) * mm});
            skLineSegment(sketch, "E391", {"start": v(-8.45, 120.4) * mm, "end": v(-8.76, 120.69) * mm});
            skLineSegment(sketch, "E392", {"start": v(-8.76, 120.69) * mm, "end": v(-9.06, 120.98) * mm});
            skLineSegment(sketch, "E393", {"start": v(-9.06, 120.98) * mm, "end": v(-9.41, 121.36) * mm});
            skLineSegment(sketch, "E394", {"start": v(-9.41, 121.36) * mm, "end": v(-9.75, 121.75) * mm});
            skLineSegment(sketch, "E395", {"start": v(-9.75, 121.75) * mm, "end": v(-10.08, 122.14) * mm});
            skLineSegment(sketch, "E396", {"start": v(-10.08, 122.14) * mm, "end": v(-10.4, 122.55) * mm});
            skLineSegment(sketch, "E397", {"start": v(-10.4, 122.55) * mm, "end": v(-10.7, 122.96) * mm});
            skLineSegment(sketch, "E398", {"start": v(-10.7, 122.96) * mm, "end": v(-11, 123.38) * mm});
            skLineSegment(sketch, "E399", {"start": v(-11, 123.38) * mm, "end": v(-11.29, 123.8) * mm});
            skLineSegment(sketch, "E400", {"start": v(-11.29, 123.8) * mm, "end": v(-11.57, 124.23) * mm});
            skLineSegment(sketch, "E401", {"start": v(-11.57, 124.23) * mm, "end": v(-11.83, 124.67) * mm});
            skLineSegment(sketch, "E402", {"start": v(-11.83, 124.67) * mm, "end": v(-12.08, 125.11) * mm});
            skLineSegment(sketch, "E403", {"start": v(-12.08, 125.11) * mm, "end": v(-12.33, 125.56) * mm});
            skLineSegment(sketch, "E404", {"start": v(-12.33, 125.56) * mm, "end": v(-12.56, 126.01) * mm});
            skLineSegment(sketch, "E405", {"start": v(-12.56, 126.01) * mm, "end": v(-12.78, 126.47) * mm});
            skLineSegment(sketch, "E406", {"start": v(-12.78, 126.47) * mm, "end": v(-12.99, 126.94) * mm});
            skLineSegment(sketch, "E407", {"start": v(-12.99, 126.94) * mm, "end": v(-13.18, 127.4) * mm});
            skLineSegment(sketch, "E408", {"start": v(-13.18, 127.4) * mm, "end": v(-13.37, 127.88) * mm});
            skLineSegment(sketch, "E409", {"start": v(-13.37, 127.88) * mm, "end": v(-13.54, 128.36) * mm});
            skLineSegment(sketch, "E410", {"start": v(-13.54, 128.36) * mm, "end": v(-13.7, 128.84) * mm});
            skLineSegment(sketch, "E411", {"start": v(-13.7, 128.84) * mm, "end": v(-13.85, 129.33) * mm});
            skLineSegment(sketch, "E412", {"start": v(-13.85, 129.33) * mm, "end": v(-14, 129.82) * mm});
            skLineSegment(sketch, "E413", {"start": v(-14, 129.82) * mm, "end": v(-14.12, 130.31) * mm});
            skLineSegment(sketch, "E414", {"start": v(-14.12, 130.31) * mm, "end": v(-14.23, 130.81) * mm});
            skLineSegment(sketch, "E415", {"start": v(-14.23, 130.81) * mm, "end": v(-14.33, 131.31) * mm});
            skLineSegment(sketch, "E416", {"start": v(-14.33, 131.31) * mm, "end": v(-14.42, 131.82) * mm});
            skLineSegment(sketch, "E417", {"start": v(-14.42, 131.82) * mm, "end": v(-14.5, 132.32) * mm});
            skLineSegment(sketch, "E418", {"start": v(-14.5, 132.32) * mm, "end": v(-14.57, 132.83) * mm});
            skLineSegment(sketch, "E419", {"start": v(-14.57, 132.83) * mm, "end": v(-14.62, 133.34) * mm});
            skLineSegment(sketch, "E420", {"start": v(-14.62, 133.34) * mm, "end": v(-14.66, 133.85) * mm});
            skLineSegment(sketch, "E421", {"start": v(-14.66, 133.85) * mm, "end": v(-14.68, 134.36) * mm});
            skLineSegment(sketch, "E422", {"start": v(-14.68, 134.36) * mm, "end": v(-14.7, 134.88) * mm});
            skLineSegment(sketch, "E423", {"start": v(-14.7, 134.88) * mm, "end": v(-14.7, 135.4) * mm});
            skLineSegment(sketch, "E424", {"start": v(-14.7, 135.4) * mm, "end": v(-14.69, 135.91) * mm});
            skLineSegment(sketch, "E425", {"start": v(-14.69, 135.91) * mm, "end": v(-14.7, 136.47) * mm});
            skLineSegment(sketch, "E426", {"start": v(-14.7, 136.47) * mm, "end": v(-14.7, 137.03) * mm});
            skLineSegment(sketch, "E427", {"start": v(-14.7, 137.03) * mm, "end": v(-14.7, 137.6) * mm});
            skLineSegment(sketch, "E428", {"start": v(-14.7, 137.6) * mm, "end": v(-14.67, 138.15) * mm});
            skLineSegment(sketch, "E429", {"start": v(-14.67, 138.15) * mm, "end": v(-14.63, 138.7) * mm});
            skLineSegment(sketch, "E430", {"start": v(-14.63, 138.7) * mm, "end": v(-14.57, 139.26) * mm});
            skLineSegment(sketch, "E431", {"start": v(-14.57, 139.26) * mm, "end": v(-14.5, 139.8) * mm});
            skLineSegment(sketch, "E432", {"start": v(-14.5, 139.8) * mm, "end": v(-14.42, 140.36) * mm});
            skLineSegment(sketch, "E433", {"start": v(-14.42, 140.36) * mm, "end": v(-14.33, 140.9) * mm});
            skLineSegment(sketch, "E434", {"start": v(-14.33, 140.9) * mm, "end": v(-14.22, 141.45) * mm});
            skLineSegment(sketch, "E435", {"start": v(-14.22, 141.45) * mm, "end": v(-14.1, 141.99) * mm});
            skLineSegment(sketch, "E436", {"start": v(-14.1, 141.99) * mm, "end": v(-13.96, 142.53) * mm});
            skLineSegment(sketch, "E437", {"start": v(-13.96, 142.53) * mm, "end": v(-13.8, 143.06) * mm});
            skLineSegment(sketch, "E438", {"start": v(-13.8, 143.06) * mm, "end": v(-13.65, 143.59) * mm});
            skLineSegment(sketch, "E439", {"start": v(-13.65, 143.59) * mm, "end": v(-13.47, 144.11) * mm});
            skLineSegment(sketch, "E440", {"start": v(-13.47, 144.11) * mm, "end": v(-13.28, 144.63) * mm});
            skLineSegment(sketch, "E441", {"start": v(-13.28, 144.63) * mm, "end": v(-13.08, 145.15) * mm});
            skLineSegment(sketch, "E442", {"start": v(-13.08, 145.15) * mm, "end": v(-12.87, 145.66) * mm});
            skLineSegment(sketch, "E443", {"start": v(-12.87, 145.66) * mm, "end": v(-12.64, 146.16) * mm});
            skLineSegment(sketch, "E444", {"start": v(-12.64, 146.16) * mm, "end": v(-12.4, 146.66) * mm});
            skLineSegment(sketch, "E445", {"start": v(-12.4, 146.66) * mm, "end": v(-12.15, 147.15) * mm});
            skLineSegment(sketch, "E446", {"start": v(-12.15, 147.15) * mm, "end": v(-11.89, 147.64) * mm});
            skLineSegment(sketch, "E447", {"start": v(-11.89, 147.64) * mm, "end": v(-11.61, 148.12) * mm});
            skLineSegment(sketch, "E448", {"start": v(-11.61, 148.12) * mm, "end": v(-11.33, 148.6) * mm});
            skLineSegment(sketch, "E449", {"start": v(-11.33, 148.6) * mm, "end": v(-11.03, 149.06) * mm});
            skLineSegment(sketch, "E450", {"start": v(-11.03, 149.06) * mm, "end": v(-10.71, 149.52) * mm});
            skLineSegment(sketch, "E451", {"start": v(-10.71, 149.52) * mm, "end": v(-10.4, 149.98) * mm});
            skLineSegment(sketch, "E452", {"start": v(-10.4, 149.98) * mm, "end": v(-10.05, 150.42) * mm});
            skLineSegment(sketch, "E453", {"start": v(-10.05, 150.42) * mm, "end": v(-9.7, 150.86) * mm});
            skLineSegment(sketch, "E454", {"start": v(-9.7, 150.86) * mm, "end": v(-9.35, 151.29) * mm});
            skLineSegment(sketch, "E455", {"start": v(-9.35, 151.29) * mm, "end": v(-8.98, 151.7) * mm});
            skLineSegment(sketch, "E456", {"start": v(-8.98, 151.7) * mm, "end": v(-8.6, 152.12) * mm});
            skLineSegment(sketch, "E457", {"start": v(-8.6, 152.12) * mm, "end": v(-8.31, 152.4) * mm});
            skLineSegment(sketch, "E458", {"start": v(-8.31, 152.4) * mm, "end": v(-8.02, 152.7) * mm});
            skLineSegment(sketch, "E459", {"start": v(-8.02, 152.7) * mm, "end": v(-7.72, 152.97) * mm});
            skLineSegment(sketch, "E460", {"start": v(-7.72, 152.97) * mm, "end": v(-7.41, 153.23) * mm});
            skLineSegment(sketch, "E461", {"start": v(-7.41, 153.23) * mm, "end": v(-7.1, 153.49) * mm});
            skLineSegment(sketch, "E462", {"start": v(-7.1, 153.49) * mm, "end": v(-6.78, 153.74) * mm});
            skLineSegment(sketch, "E463", {"start": v(-6.78, 153.74) * mm, "end": v(-6.46, 153.98) * mm});
            skLineSegment(sketch, "E464", {"start": v(-6.46, 153.98) * mm, "end": v(-6.13, 154.2) * mm});
            skLineSegment(sketch, "E465", {"start": v(-6.13, 154.2) * mm, "end": v(-5.8, 154.43) * mm});
            skLineSegment(sketch, "E466", {"start": v(-5.8, 154.43) * mm, "end": v(-5.45, 154.65) * mm});
            skLineSegment(sketch, "E467", {"start": v(-5.45, 154.65) * mm, "end": v(-5.1, 154.85) * mm});
            skLineSegment(sketch, "E468", {"start": v(-5.1, 154.85) * mm, "end": v(-4.76, 155.05) * mm});
            skLineSegment(sketch, "E469", {"start": v(-4.76, 155.05) * mm, "end": v(-4.4, 155.23) * mm});
            skLineSegment(sketch, "E470", {"start": v(-4.4, 155.23) * mm, "end": v(-4.04, 155.41) * mm});
            skLineSegment(sketch, "E471", {"start": v(-4.04, 155.41) * mm, "end": v(-3.68, 155.58) * mm});
            skLineSegment(sketch, "E472", {"start": v(-3.68, 155.58) * mm, "end": v(-3.31, 155.74) * mm});
            skLineSegment(sketch, "E473", {"start": v(-3.31, 155.74) * mm, "end": v(-2.94, 155.89) * mm});
            skLineSegment(sketch, "E474", {"start": v(-2.94, 155.89) * mm, "end": v(-2.56, 156.03) * mm});
            skLineSegment(sketch, "E475", {"start": v(-2.56, 156.03) * mm, "end": v(-2.18, 156.16) * mm});
            skLineSegment(sketch, "E476", {"start": v(-2.18, 156.16) * mm, "end": v(-1.8, 156.28) * mm});
            skLineSegment(sketch, "E477", {"start": v(-1.8, 156.28) * mm, "end": v(-1.41, 156.4) * mm});
            skLineSegment(sketch, "E478", {"start": v(-1.41, 156.4) * mm, "end": v(-1.03, 156.5) * mm});
            skLineSegment(sketch, "E479", {"start": v(-1.03, 156.5) * mm, "end": v(-0.63, 156.58) * mm});
            skLineSegment(sketch, "E480", {"start": v(-0.63, 156.58) * mm, "end": v(-0.24, 156.66) * mm});
            skLineSegment(sketch, "E481", {"start": v(-0.24, 156.66) * mm, "end": v(0.16, 156.74) * mm});
            skLineSegment(sketch, "E482", {"start": v(0.16, 156.74) * mm, "end": v(0.56, 156.8) * mm});
            skLineSegment(sketch, "E483", {"start": v(0.56, 156.8) * mm, "end": v(0.96, 156.85) * mm});
            skLineSegment(sketch, "E484", {"start": v(0.96, 156.85) * mm, "end": v(1.36, 156.89) * mm});
            skLineSegment(sketch, "E485", {"start": v(1.36, 156.89) * mm, "end": v(1.76, 156.92) * mm});
            skLineSegment(sketch, "E486", {"start": v(1.76, 156.92) * mm, "end": v(2.17, 156.94) * mm});
            skLineSegment(sketch, "E487", {"start": v(2.17, 156.94) * mm, "end": v(2.57, 156.95) * mm});
            skLineSegment(sketch, "E488", {"start": v(2.57, 156.95) * mm, "end": v(2.98, 156.95) * mm});
            skLineSegment(sketch, "E489", {"start": v(2.98, 156.95) * mm, "end": v(3.4, 156.94) * mm});
            skLineSegment(sketch, "E490", {"start": v(3.4, 156.94) * mm, "end": v(3.8, 156.93) * mm});
            skLineSegment(sketch, "E491", {"start": v(3.8, 156.93) * mm, "end": v(4.22, 156.9) * mm});
            skLineSegment(sketch, "E492", {"start": v(4.22, 156.9) * mm, "end": v(4.63, 156.87) * mm});
            skLineSegment(sketch, "E493", {"start": v(4.63, 156.87) * mm, "end": v(5.04, 156.82) * mm});
            skLineSegment(sketch, "E494", {"start": v(5.04, 156.82) * mm, "end": v(5.45, 156.76) * mm});
            skLineSegment(sketch, "E495", {"start": v(5.45, 156.76) * mm, "end": v(5.85, 156.7) * mm});
            skLineSegment(sketch, "E496", {"start": v(5.85, 156.7) * mm, "end": v(6.25, 156.62) * mm});
            skLineSegment(sketch, "E497", {"start": v(6.25, 156.62) * mm, "end": v(6.65, 156.53) * mm});
            skLineSegment(sketch, "E498", {"start": v(6.65, 156.53) * mm, "end": v(7.05, 156.43) * mm});
            skLineSegment(sketch, "E499", {"start": v(7.05, 156.43) * mm, "end": v(7.44, 156.33) * mm});
            skLineSegment(sketch, "E500", {"start": v(7.44, 156.33) * mm, "end": v(7.83, 156.2) * mm});
            skLineSegment(sketch, "E501", {"start": v(7.83, 156.2) * mm, "end": v(8.22, 156.08) * mm});
            skLineSegment(sketch, "E502", {"start": v(8.22, 156.08) * mm, "end": v(8.6, 155.94) * mm});
            skLineSegment(sketch, "E503", {"start": v(8.6, 155.94) * mm, "end": v(8.99, 155.8) * mm});
            skLineSegment(sketch, "E504", {"start": v(8.99, 155.8) * mm, "end": v(9.36, 155.64) * mm});
            skLineSegment(sketch, "E505", {"start": v(9.36, 155.64) * mm, "end": v(9.73, 155.47) * mm});
            skLineSegment(sketch, "E506", {"start": v(9.73, 155.47) * mm, "end": v(10.1, 155.3) * mm});
            skLineSegment(sketch, "E507", {"start": v(10.1, 155.3) * mm, "end": v(10.47, 155.11) * mm});
            skLineSegment(sketch, "E508", {"start": v(10.47, 155.11) * mm, "end": v(10.83, 154.92) * mm});
            skLineSegment(sketch, "E509", {"start": v(10.83, 154.92) * mm, "end": v(11.18, 154.71) * mm});
            skLineSegment(sketch, "E510", {"start": v(11.18, 154.71) * mm, "end": v(11.53, 154.5) * mm});
            skLineSegment(sketch, "E511", {"start": v(11.53, 154.5) * mm, "end": v(11.87, 154.28) * mm});
            skLineSegment(sketch, "E512", {"start": v(11.87, 154.28) * mm, "end": v(12.2, 154.05) * mm});
            skLineSegment(sketch, "E513", {"start": v(12.2, 154.05) * mm, "end": v(12.54, 153.81) * mm});
            skLineSegment(sketch, "E514", {"start": v(12.54, 153.81) * mm, "end": v(12.87, 153.56) * mm});
            skLineSegment(sketch, "E515", {"start": v(12.87, 153.56) * mm, "end": v(13.19, 153.3) * mm});
            skLineSegment(sketch, "E516", {"start": v(13.19, 153.3) * mm, "end": v(13.5, 153.04) * mm});
            skLineSegment(sketch, "E517", {"start": v(13.5, 153.04) * mm, "end": v(13.8, 152.77) * mm});
            skLineSegment(sketch, "E518", {"start": v(13.8, 152.77) * mm, "end": v(14.11, 152.48) * mm});
            skLineSegment(sketch, "E519", {"start": v(14.11, 152.48) * mm, "end": v(14.4, 152.2) * mm});
            skLineSegment(sketch, "E520", {"start": v(14.4, 152.2) * mm, "end": v(14.7, 151.9) * mm});
            skLineSegment(sketch, "E521", {"start": v(14.7, 151.9) * mm, "end": v(15.06, 151.48) * mm});
            skLineSegment(sketch, "E522", {"start": v(15.06, 151.48) * mm, "end": v(15.42, 151.07) * mm});
            skLineSegment(sketch, "E523", {"start": v(15.42, 151.07) * mm, "end": v(15.77, 150.64) * mm});
            skLineSegment(sketch, "E524", {"start": v(15.77, 150.64) * mm, "end": v(16.1, 150.2) * mm});
            skLineSegment(sketch, "E525", {"start": v(16.1, 150.2) * mm, "end": v(16.43, 149.77) * mm});
            skLineSegment(sketch, "E526", {"start": v(16.43, 149.77) * mm, "end": v(16.74, 149.32) * mm});
            skLineSegment(sketch, "E527", {"start": v(16.74, 149.32) * mm, "end": v(17.04, 148.86) * mm});
            skLineSegment(sketch, "E528", {"start": v(17.04, 148.86) * mm, "end": v(17.33, 148.4) * mm});
            skLineSegment(sketch, "E529", {"start": v(17.33, 148.4) * mm, "end": v(17.61, 147.93) * mm});
            skLineSegment(sketch, "E530", {"start": v(17.61, 147.93) * mm, "end": v(17.88, 147.45) * mm});
            skLineSegment(sketch, "E531", {"start": v(17.88, 147.45) * mm, "end": v(18.13, 146.97) * mm});
            skLineSegment(sketch, "E532", {"start": v(18.13, 146.97) * mm, "end": v(18.37, 146.48) * mm});
            skLineSegment(sketch, "E533", {"start": v(18.37, 146.48) * mm, "end": v(18.6, 145.99) * mm});
            skLineSegment(sketch, "E534", {"start": v(18.6, 145.99) * mm, "end": v(18.82, 145.49) * mm});
            skLineSegment(sketch, "E535", {"start": v(18.82, 145.49) * mm, "end": v(19.03, 144.99) * mm});
            skLineSegment(sketch, "E536", {"start": v(19.03, 144.99) * mm, "end": v(19.22, 144.48) * mm});
            skLineSegment(sketch, "E537", {"start": v(19.22, 144.48) * mm, "end": v(19.4, 143.96) * mm});
            skLineSegment(sketch, "E538", {"start": v(19.4, 143.96) * mm, "end": v(19.57, 143.45) * mm});
            skLineSegment(sketch, "E539", {"start": v(19.57, 143.45) * mm, "end": v(19.72, 142.92) * mm});
            skLineSegment(sketch, "E540", {"start": v(19.72, 142.92) * mm, "end": v(19.86, 142.4) * mm});
            skLineSegment(sketch, "E541", {"start": v(19.86, 142.4) * mm, "end": v(20, 141.87) * mm});
            skLineSegment(sketch, "E542", {"start": v(20, 141.87) * mm, "end": v(20.1, 141.34) * mm});
            skLineSegment(sketch, "E543", {"start": v(20.1, 141.34) * mm, "end": v(20.2, 140.8) * mm});
            skLineSegment(sketch, "E544", {"start": v(20.2, 140.8) * mm, "end": v(20.3, 140.26) * mm});
            skLineSegment(sketch, "E545", {"start": v(20.3, 140.26) * mm, "end": v(20.37, 139.72) * mm});
            skLineSegment(sketch, "E546", {"start": v(20.37, 139.72) * mm, "end": v(20.44, 139.18) * mm});
            skLineSegment(sketch, "E547", {"start": v(20.44, 139.18) * mm, "end": v(20.49, 138.63) * mm});
            skLineSegment(sketch, "E548", {"start": v(20.49, 138.63) * mm, "end": v(20.52, 138.09) * mm});
            skLineSegment(sketch, "E549", {"start": v(20.52, 138.09) * mm, "end": v(20.54, 137.54) * mm});
            skLineSegment(sketch, "E550", {"start": v(20.54, 137.54) * mm, "end": v(20.55, 136.99) * mm});
            skLineSegment(sketch, "E551", {"start": v(20.55, 136.99) * mm, "end": v(20.55, 136.44) * mm});
            skLineSegment(sketch, "E552", {"start": v(20.55, 136.44) * mm, "end": v(20.53, 135.89) * mm});
            skLineSegment(sketch, "E553", {"start": v(20.53, 135.89) * mm, "end": v(20.53, 135.37) * mm});
            skLineSegment(sketch, "E554", {"start": v(20.53, 135.37) * mm, "end": v(20.53, 134.86) * mm});
            skLineSegment(sketch, "E555", {"start": v(20.53, 134.86) * mm, "end": v(20.51, 134.35) * mm});
            skLineSegment(sketch, "E556", {"start": v(20.51, 134.35) * mm, "end": v(20.48, 133.83) * mm});
            skLineSegment(sketch, "E557", {"start": v(20.48, 133.83) * mm, "end": v(20.44, 133.32) * mm});
            skLineSegment(sketch, "E558", {"start": v(20.44, 133.32) * mm, "end": v(20.38, 132.82) * mm});
            skLineSegment(sketch, "E559", {"start": v(20.38, 132.82) * mm, "end": v(20.31, 132.31) * mm});
            skLineSegment(sketch, "E560", {"start": v(20.31, 132.31) * mm, "end": v(20.23, 131.8) * mm});
            skLineSegment(sketch, "E561", {"start": v(20.23, 131.8) * mm, "end": v(20.14, 131.3) * mm});
            skLineSegment(sketch, "E562", {"start": v(20.14, 131.3) * mm, "end": v(20.03, 130.81) * mm});
            skLineSegment(sketch, "E563", {"start": v(20.03, 130.81) * mm, "end": v(19.91, 130.32) * mm});
            skLineSegment(sketch, "E564", {"start": v(19.91, 130.32) * mm, "end": v(19.78, 129.83) * mm});
            skLineSegment(sketch, "E565", {"start": v(19.78, 129.83) * mm, "end": v(19.64, 129.34) * mm});
            skLineSegment(sketch, "E566", {"start": v(19.64, 129.34) * mm, "end": v(19.49, 128.86) * mm});
            skLineSegment(sketch, "E567", {"start": v(19.49, 128.86) * mm, "end": v(19.32, 128.38) * mm});
            skLineSegment(sketch, "E568", {"start": v(19.32, 128.38) * mm, "end": v(19.14, 127.9) * mm});
            skLineSegment(sketch, "E569", {"start": v(19.14, 127.9) * mm, "end": v(18.95, 127.43) * mm});
            skLineSegment(sketch, "E570", {"start": v(18.95, 127.43) * mm, "end": v(18.75, 126.97) * mm});
            skLineSegment(sketch, "E571", {"start": v(18.75, 126.97) * mm, "end": v(18.54, 126.5) * mm});
            skLineSegment(sketch, "E572", {"start": v(18.54, 126.5) * mm, "end": v(18.31, 126.05) * mm});
            skLineSegment(sketch, "E573", {"start": v(18.31, 126.05) * mm, "end": v(18.08, 125.6) * mm});
            skLineSegment(sketch, "E574", {"start": v(18.08, 125.6) * mm, "end": v(17.83, 125.16) * mm});
            skLineSegment(sketch, "E575", {"start": v(17.83, 125.16) * mm, "end": v(17.57, 124.72) * mm});
            skLineSegment(sketch, "E576", {"start": v(17.57, 124.72) * mm, "end": v(17.3, 124.29) * mm});
            skLineSegment(sketch, "E577", {"start": v(17.3, 124.29) * mm, "end": v(17.02, 123.86) * mm});
            skLineSegment(sketch, "E578", {"start": v(17.02, 123.86) * mm, "end": v(16.73, 123.44) * mm});
            skLineSegment(sketch, "E579", {"start": v(16.73, 123.44) * mm, "end": v(16.43, 123.03) * mm});
            skLineSegment(sketch, "E580", {"start": v(16.43, 123.03) * mm, "end": v(16.12, 122.63) * mm});
            skLineSegment(sketch, "E581", {"start": v(16.12, 122.63) * mm, "end": v(15.8, 122.23) * mm});
            skLineSegment(sketch, "E582", {"start": v(15.8, 122.23) * mm, "end": v(15.46, 121.84) * mm});
            skLineSegment(sketch, "E583", {"start": v(15.46, 121.84) * mm, "end": v(15.12, 121.46) * mm});
            skLineSegment(sketch, "E584", {"start": v(15.12, 121.46) * mm, "end": v(14.76, 121.08) * mm});
            skLineSegment(sketch, "E585", {"start": v(14.76, 121.08) * mm, "end": v(14.47, 120.8) * mm});
            skLineSegment(sketch, "E586", {"start": v(14.47, 120.8) * mm, "end": v(14.17, 120.5) * mm});
            skLineSegment(sketch, "E587", {"start": v(14.17, 120.5) * mm, "end": v(13.86, 120.23) * mm});
            skLineSegment(sketch, "E588", {"start": v(13.86, 120.23) * mm, "end": v(13.55, 119.97) * mm});
            skLineSegment(sketch, "E589", {"start": v(13.55, 119.97) * mm, "end": v(13.23, 119.7) * mm});
            skLineSegment(sketch, "E590", {"start": v(13.23, 119.7) * mm, "end": v(12.9, 119.46) * mm});
            skLineSegment(sketch, "E591", {"start": v(12.9, 119.46) * mm, "end": v(12.57, 119.22) * mm});
            skLineSegment(sketch, "E592", {"start": v(12.57, 119.22) * mm, "end": v(12.24, 118.99) * mm});
            skLineSegment(sketch, "E593", {"start": v(12.24, 118.99) * mm, "end": v(11.9, 118.76) * mm});
            skLineSegment(sketch, "E594", {"start": v(11.9, 118.76) * mm, "end": v(11.55, 118.55) * mm});
            skLineSegment(sketch, "E595", {"start": v(11.55, 118.55) * mm, "end": v(11.2, 118.34) * mm});
            skLineSegment(sketch, "E596", {"start": v(11.2, 118.34) * mm, "end": v(10.84, 118.14) * mm});
            skLineSegment(sketch, "E597", {"start": v(10.84, 118.14) * mm, "end": v(10.47, 117.95) * mm});
            skLineSegment(sketch, "E598", {"start": v(10.47, 117.95) * mm, "end": v(10.1, 117.77) * mm});
            skLineSegment(sketch, "E599", {"start": v(10.1, 117.77) * mm, "end": v(9.74, 117.6) * mm});
            skLineSegment(sketch, "E600", {"start": v(9.74, 117.6) * mm, "end": v(9.36, 117.44) * mm});
            skLineSegment(sketch, "E601", {"start": v(9.36, 117.44) * mm, "end": v(8.99, 117.3) * mm});
            skLineSegment(sketch, "E602", {"start": v(8.99, 117.3) * mm, "end": v(8.6, 117.15) * mm});
            skLineSegment(sketch, "E603", {"start": v(8.6, 117.15) * mm, "end": v(8.22, 117.02) * mm});
            skLineSegment(sketch, "E604", {"start": v(8.22, 117.02) * mm, "end": v(7.83, 116.9) * mm});
            skLineSegment(sketch, "E605", {"start": v(7.83, 116.9) * mm, "end": v(7.44, 116.78) * mm});
            skLineSegment(sketch, "E606", {"start": v(7.44, 116.78) * mm, "end": v(7.04, 116.68) * mm});
            skLineSegment(sketch, "E607", {"start": v(7.04, 116.68) * mm, "end": v(6.64, 116.58) * mm});
            skLineSegment(sketch, "E608", {"start": v(6.64, 116.58) * mm, "end": v(6.24, 116.5) * mm});
            skLineSegment(sketch, "E609", {"start": v(6.24, 116.5) * mm, "end": v(5.84, 116.42) * mm});
            skLineSegment(sketch, "E610", {"start": v(5.84, 116.42) * mm, "end": v(5.44, 116.36) * mm});
            skLineSegment(sketch, "E611", {"start": v(5.44, 116.36) * mm, "end": v(5.03, 116.3) * mm});
            skLineSegment(sketch, "E612", {"start": v(5.03, 116.3) * mm, "end": v(4.62, 116.26) * mm});
            skLineSegment(sketch, "E613", {"start": v(4.62, 116.26) * mm, "end": v(4.21, 116.22) * mm});
            skLineSegment(sketch, "E614", {"start": v(4.21, 116.22) * mm, "end": v(3.8, 116.2) * mm});
            skLineSegment(sketch, "E615", {"start": v(3.8, 116.2) * mm, "end": v(3.39, 116.19) * mm});
            skLineSegment(sketch, "E616", {"start": v(3.39, 116.19) * mm, "end": v(2.97, 116.19) * mm});
            skLineSegment(sketch, "E617", {"start": v(47.22, 116.19) * mm, "end": v(46.8, 116.18) * mm});
            skLineSegment(sketch, "E618", {"start": v(46.8, 116.18) * mm, "end": v(46.38, 116.19) * mm});
            skLineSegment(sketch, "E619", {"start": v(46.38, 116.19) * mm, "end": v(45.96, 116.2) * mm});
            skLineSegment(sketch, "E620", {"start": v(45.96, 116.2) * mm, "end": v(45.55, 116.23) * mm});
            skLineSegment(sketch, "E621", {"start": v(45.55, 116.23) * mm, "end": v(45.13, 116.27) * mm});
            skLineSegment(sketch, "E622", {"start": v(45.13, 116.27) * mm, "end": v(44.72, 116.32) * mm});
            skLineSegment(sketch, "E623", {"start": v(44.72, 116.32) * mm, "end": v(44.3, 116.38) * mm});
            skLineSegment(sketch, "E624", {"start": v(44.3, 116.38) * mm, "end": v(43.9, 116.45) * mm});
            skLineSegment(sketch, "E625", {"start": v(43.9, 116.45) * mm, "end": v(43.49, 116.53) * mm});
            skLineSegment(sketch, "E626", {"start": v(43.49, 116.53) * mm, "end": v(43.08, 116.62) * mm});
            skLineSegment(sketch, "E627", {"start": v(43.08, 116.62) * mm, "end": v(42.68, 116.72) * mm});
            skLineSegment(sketch, "E628", {"start": v(42.68, 116.72) * mm, "end": v(42.28, 116.83) * mm});
            skLineSegment(sketch, "E629", {"start": v(42.28, 116.83) * mm, "end": v(41.89, 116.95) * mm});
            skLineSegment(sketch, "E630", {"start": v(41.89, 116.95) * mm, "end": v(41.5, 117.08) * mm});
            skLineSegment(sketch, "E631", {"start": v(41.5, 117.08) * mm, "end": v(41.1, 117.22) * mm});
            skLineSegment(sketch, "E632", {"start": v(41.1, 117.22) * mm, "end": v(40.72, 117.37) * mm});
            skLineSegment(sketch, "E633", {"start": v(40.72, 117.37) * mm, "end": v(40.33, 117.52) * mm});
            skLineSegment(sketch, "E634", {"start": v(40.33, 117.52) * mm, "end": v(39.96, 117.7) * mm});
            skLineSegment(sketch, "E635", {"start": v(39.96, 117.7) * mm, "end": v(39.58, 117.87) * mm});
            skLineSegment(sketch, "E636", {"start": v(39.58, 117.87) * mm, "end": v(39.21, 118.05) * mm});
            skLineSegment(sketch, "E637", {"start": v(39.21, 118.05) * mm, "end": v(38.85, 118.25) * mm});
            skLineSegment(sketch, "E638", {"start": v(38.85, 118.25) * mm, "end": v(38.49, 118.45) * mm});
            skLineSegment(sketch, "E639", {"start": v(38.49, 118.45) * mm, "end": v(38.13, 118.67) * mm});
            skLineSegment(sketch, "E640", {"start": v(38.13, 118.67) * mm, "end": v(37.78, 118.89) * mm});
            skLineSegment(sketch, "E641", {"start": v(37.78, 118.89) * mm, "end": v(37.43, 119.12) * mm});
            skLineSegment(sketch, "E642", {"start": v(37.43, 119.12) * mm, "end": v(37.1, 119.36) * mm});
            skLineSegment(sketch, "E643", {"start": v(37.1, 119.36) * mm, "end": v(36.76, 119.6) * mm});
            skLineSegment(sketch, "E644", {"start": v(36.76, 119.6) * mm, "end": v(36.43, 119.86) * mm});
            skLineSegment(sketch, "E645", {"start": v(36.43, 119.86) * mm, "end": v(36.11, 120.13) * mm});
            skLineSegment(sketch, "E646", {"start": v(36.11, 120.13) * mm, "end": v(35.8, 120.4) * mm});
            skLineSegment(sketch, "E647", {"start": v(35.8, 120.4) * mm, "end": v(35.49, 120.69) * mm});
            skLineSegment(sketch, "E648", {"start": v(35.49, 120.69) * mm, "end": v(35.18, 120.98) * mm});
            skLineSegment(sketch, "E649", {"start": v(35.18, 120.98) * mm, "end": v(34.83, 121.36) * mm});
            skLineSegment(sketch, "E650", {"start": v(34.83, 121.36) * mm, "end": v(34.5, 121.75) * mm});
            skLineSegment(sketch, "E651", {"start": v(34.5, 121.75) * mm, "end": v(34.17, 122.14) * mm});
            skLineSegment(sketch, "E652", {"start": v(34.17, 122.14) * mm, "end": v(33.85, 122.55) * mm});
            skLineSegment(sketch, "E653", {"start": v(33.85, 122.55) * mm, "end": v(33.54, 122.96) * mm});
            skLineSegment(sketch, "E654", {"start": v(33.54, 122.96) * mm, "end": v(33.24, 123.38) * mm});
            skLineSegment(sketch, "E655", {"start": v(33.24, 123.38) * mm, "end": v(32.96, 123.8) * mm});
            skLineSegment(sketch, "E656", {"start": v(32.96, 123.8) * mm, "end": v(32.68, 124.23) * mm});
            skLineSegment(sketch, "E657", {"start": v(32.68, 124.23) * mm, "end": v(32.42, 124.67) * mm});
            skLineSegment(sketch, "E658", {"start": v(32.42, 124.67) * mm, "end": v(32.16, 125.11) * mm});
            skLineSegment(sketch, "E659", {"start": v(32.16, 125.11) * mm, "end": v(31.92, 125.56) * mm});
            skLineSegment(sketch, "E660", {"start": v(31.92, 125.56) * mm, "end": v(31.69, 126.01) * mm});
            skLineSegment(sketch, "E661", {"start": v(31.69, 126.01) * mm, "end": v(31.47, 126.47) * mm});
            skLineSegment(sketch, "E662", {"start": v(31.47, 126.47) * mm, "end": v(31.26, 126.94) * mm});
            skLineSegment(sketch, "E663", {"start": v(31.26, 126.94) * mm, "end": v(31.06, 127.4) * mm});
            skLineSegment(sketch, "E664", {"start": v(31.06, 127.4) * mm, "end": v(30.88, 127.88) * mm});
            skLineSegment(sketch, "E665", {"start": v(30.88, 127.88) * mm, "end": v(30.7, 128.36) * mm});
            skLineSegment(sketch, "E666", {"start": v(30.7, 128.36) * mm, "end": v(30.54, 128.84) * mm});
            skLineSegment(sketch, "E667", {"start": v(30.54, 128.84) * mm, "end": v(30.4, 129.33) * mm});
            skLineSegment(sketch, "E668", {"start": v(30.4, 129.33) * mm, "end": v(30.25, 129.82) * mm});
            skLineSegment(sketch, "E669", {"start": v(30.25, 129.82) * mm, "end": v(30.13, 130.31) * mm});
            skLineSegment(sketch, "E670", {"start": v(30.13, 130.31) * mm, "end": v(30.01, 130.81) * mm});
            skLineSegment(sketch, "E671", {"start": v(30.01, 130.81) * mm, "end": v(29.91, 131.31) * mm});
            skLineSegment(sketch, "E672", {"start": v(29.91, 131.31) * mm, "end": v(29.82, 131.82) * mm});
            skLineSegment(sketch, "E673", {"start": v(29.82, 131.82) * mm, "end": v(29.74, 132.32) * mm});
            skLineSegment(sketch, "E674", {"start": v(29.74, 132.32) * mm, "end": v(29.68, 132.83) * mm});
            skLineSegment(sketch, "E675", {"start": v(29.68, 132.83) * mm, "end": v(29.63, 133.34) * mm});
            skLineSegment(sketch, "E676", {"start": v(29.63, 133.34) * mm, "end": v(29.59, 133.85) * mm});
            skLineSegment(sketch, "E677", {"start": v(29.59, 133.85) * mm, "end": v(29.56, 134.36) * mm});
            skLineSegment(sketch, "E678", {"start": v(29.56, 134.36) * mm, "end": v(29.55, 134.88) * mm});
            skLineSegment(sketch, "E679", {"start": v(29.55, 134.88) * mm, "end": v(29.55, 135.4) * mm});
            skLineSegment(sketch, "E680", {"start": v(29.55, 135.4) * mm, "end": v(29.56, 135.91) * mm});
            skLineSegment(sketch, "E681", {"start": v(29.56, 135.91) * mm, "end": v(29.54, 136.47) * mm});
            skLineSegment(sketch, "E682", {"start": v(29.54, 136.47) * mm, "end": v(29.54, 137.03) * mm});
            skLineSegment(sketch, "E683", {"start": v(29.54, 137.03) * mm, "end": v(29.55, 137.6) * mm});
            skLineSegment(sketch, "E684", {"start": v(29.55, 137.6) * mm, "end": v(29.58, 138.15) * mm});
            skLineSegment(sketch, "E685", {"start": v(29.58, 138.15) * mm, "end": v(29.62, 138.7) * mm});
            skLineSegment(sketch, "E686", {"start": v(29.62, 138.7) * mm, "end": v(29.67, 139.26) * mm});
            skLineSegment(sketch, "E687", {"start": v(29.67, 139.26) * mm, "end": v(29.74, 139.8) * mm});
            skLineSegment(sketch, "E688", {"start": v(29.74, 139.8) * mm, "end": v(29.82, 140.36) * mm});
            skLineSegment(sketch, "E689", {"start": v(29.82, 140.36) * mm, "end": v(29.92, 140.9) * mm});
            skLineSegment(sketch, "E690", {"start": v(29.92, 140.9) * mm, "end": v(30.03, 141.45) * mm});
            skLineSegment(sketch, "E691", {"start": v(30.03, 141.45) * mm, "end": v(30.15, 141.99) * mm});
            skLineSegment(sketch, "E692", {"start": v(30.15, 141.99) * mm, "end": v(30.29, 142.53) * mm});
            skLineSegment(sketch, "E693", {"start": v(30.29, 142.53) * mm, "end": v(30.44, 143.06) * mm});
            skLineSegment(sketch, "E694", {"start": v(30.44, 143.06) * mm, "end": v(30.6, 143.59) * mm});
            skLineSegment(sketch, "E695", {"start": v(30.6, 143.59) * mm, "end": v(30.77, 144.11) * mm});
            skLineSegment(sketch, "E696", {"start": v(30.77, 144.11) * mm, "end": v(30.96, 144.63) * mm});
            skLineSegment(sketch, "E697", {"start": v(30.96, 144.63) * mm, "end": v(31.16, 145.15) * mm});
            skLineSegment(sketch, "E698", {"start": v(31.16, 145.15) * mm, "end": v(31.38, 145.66) * mm});
            skLineSegment(sketch, "E699", {"start": v(31.38, 145.66) * mm, "end": v(31.6, 146.16) * mm});
            skLineSegment(sketch, "E700", {"start": v(31.6, 146.16) * mm, "end": v(31.84, 146.66) * mm});
            skLineSegment(sketch, "E701", {"start": v(31.84, 146.66) * mm, "end": v(32.1, 147.15) * mm});
            skLineSegment(sketch, "E702", {"start": v(32.1, 147.15) * mm, "end": v(32.36, 147.64) * mm});
            skLineSegment(sketch, "E703", {"start": v(32.36, 147.64) * mm, "end": v(32.63, 148.12) * mm});
            skLineSegment(sketch, "E704", {"start": v(32.63, 148.12) * mm, "end": v(32.92, 148.6) * mm});
            skLineSegment(sketch, "E705", {"start": v(32.92, 148.6) * mm, "end": v(33.22, 149.06) * mm});
            skLineSegment(sketch, "E706", {"start": v(33.22, 149.06) * mm, "end": v(33.53, 149.52) * mm});
            skLineSegment(sketch, "E707", {"start": v(33.53, 149.52) * mm, "end": v(33.86, 149.98) * mm});
            skLineSegment(sketch, "E708", {"start": v(33.86, 149.98) * mm, "end": v(34.2, 150.42) * mm});
            skLineSegment(sketch, "E709", {"start": v(34.2, 150.42) * mm, "end": v(34.54, 150.86) * mm});
            skLineSegment(sketch, "E710", {"start": v(34.54, 150.86) * mm, "end": v(34.9, 151.29) * mm});
            skLineSegment(sketch, "E711", {"start": v(34.9, 151.29) * mm, "end": v(35.27, 151.7) * mm});
            skLineSegment(sketch, "E712", {"start": v(35.27, 151.7) * mm, "end": v(35.65, 152.12) * mm});
            skLineSegment(sketch, "E713", {"start": v(35.65, 152.12) * mm, "end": v(35.93, 152.4) * mm});
            skLineSegment(sketch, "E714", {"start": v(35.93, 152.4) * mm, "end": v(36.23, 152.7) * mm});
            skLineSegment(sketch, "E715", {"start": v(36.23, 152.7) * mm, "end": v(36.53, 152.97) * mm});
            skLineSegment(sketch, "E716", {"start": v(36.53, 152.97) * mm, "end": v(36.83, 153.23) * mm});
            skLineSegment(sketch, "E717", {"start": v(36.83, 153.23) * mm, "end": v(37.14, 153.49) * mm});
            skLineSegment(sketch, "E718", {"start": v(37.14, 153.49) * mm, "end": v(37.46, 153.74) * mm});
            skLineSegment(sketch, "E719", {"start": v(37.46, 153.74) * mm, "end": v(37.79, 153.98) * mm});
            skLineSegment(sketch, "E720", {"start": v(37.79, 153.98) * mm, "end": v(38.12, 154.2) * mm});
            skLineSegment(sketch, "E721", {"start": v(38.12, 154.2) * mm, "end": v(38.45, 154.43) * mm});
            skLineSegment(sketch, "E722", {"start": v(38.45, 154.43) * mm, "end": v(38.8, 154.65) * mm});
            skLineSegment(sketch, "E723", {"start": v(38.8, 154.65) * mm, "end": v(39.14, 154.85) * mm});
            skLineSegment(sketch, "E724", {"start": v(39.14, 154.85) * mm, "end": v(39.49, 155.05) * mm});
            skLineSegment(sketch, "E725", {"start": v(39.49, 155.05) * mm, "end": v(39.84, 155.23) * mm});
            skLineSegment(sketch, "E726", {"start": v(39.84, 155.23) * mm, "end": v(40.2, 155.41) * mm});
            skLineSegment(sketch, "E727", {"start": v(40.2, 155.41) * mm, "end": v(40.57, 155.58) * mm});
            skLineSegment(sketch, "E728", {"start": v(40.57, 155.58) * mm, "end": v(40.93, 155.74) * mm});
            skLineSegment(sketch, "E729", {"start": v(40.93, 155.74) * mm, "end": v(41.3, 155.89) * mm});
            skLineSegment(sketch, "E730", {"start": v(41.3, 155.89) * mm, "end": v(41.68, 156.03) * mm});
            skLineSegment(sketch, "E731", {"start": v(41.68, 156.03) * mm, "end": v(42.06, 156.16) * mm});
            skLineSegment(sketch, "E732", {"start": v(42.06, 156.16) * mm, "end": v(42.44, 156.28) * mm});
            skLineSegment(sketch, "E733", {"start": v(42.44, 156.28) * mm, "end": v(42.83, 156.4) * mm});
            skLineSegment(sketch, "E734", {"start": v(42.83, 156.4) * mm, "end": v(43.22, 156.5) * mm});
            skLineSegment(sketch, "E735", {"start": v(43.22, 156.5) * mm, "end": v(43.61, 156.58) * mm});
            skLineSegment(sketch, "E736", {"start": v(43.61, 156.58) * mm, "end": v(44, 156.66) * mm});
            skLineSegment(sketch, "E737", {"start": v(44, 156.66) * mm, "end": v(44.4, 156.74) * mm});
            skLineSegment(sketch, "E738", {"start": v(44.4, 156.74) * mm, "end": v(44.8, 156.8) * mm});
            skLineSegment(sketch, "E739", {"start": v(44.8, 156.8) * mm, "end": v(45.2, 156.85) * mm});
            skLineSegment(sketch, "E740", {"start": v(45.2, 156.85) * mm, "end": v(45.6, 156.89) * mm});
            skLineSegment(sketch, "E741", {"start": v(45.6, 156.89) * mm, "end": v(46, 156.92) * mm});
            skLineSegment(sketch, "E742", {"start": v(46, 156.92) * mm, "end": v(46.41, 156.94) * mm});
            skLineSegment(sketch, "E743", {"start": v(46.41, 156.94) * mm, "end": v(46.82, 156.95) * mm});
            skLineSegment(sketch, "E744", {"start": v(46.82, 156.95) * mm, "end": v(47.23, 156.95) * mm});
            skLineSegment(sketch, "E745", {"start": v(47.23, 156.95) * mm, "end": v(47.64, 156.94) * mm});
            skLineSegment(sketch, "E746", {"start": v(47.64, 156.94) * mm, "end": v(48.05, 156.93) * mm});
            skLineSegment(sketch, "E747", {"start": v(48.05, 156.93) * mm, "end": v(48.47, 156.9) * mm});
            skLineSegment(sketch, "E748", {"start": v(48.47, 156.9) * mm, "end": v(48.88, 156.87) * mm});
            skLineSegment(sketch, "E749", {"start": v(48.88, 156.87) * mm, "end": v(49.29, 156.82) * mm});
            skLineSegment(sketch, "E750", {"start": v(49.29, 156.82) * mm, "end": v(49.7, 156.76) * mm});
            skLineSegment(sketch, "E751", {"start": v(49.7, 156.76) * mm, "end": v(50.1, 156.7) * mm});
            skLineSegment(sketch, "E752", {"start": v(50.1, 156.7) * mm, "end": v(50.5, 156.62) * mm});
            skLineSegment(sketch, "E753", {"start": v(50.5, 156.62) * mm, "end": v(50.9, 156.53) * mm});
            skLineSegment(sketch, "E754", {"start": v(50.9, 156.53) * mm, "end": v(51.3, 156.43) * mm});
            skLineSegment(sketch, "E755", {"start": v(51.3, 156.43) * mm, "end": v(51.69, 156.33) * mm});
            skLineSegment(sketch, "E756", {"start": v(51.69, 156.33) * mm, "end": v(52.08, 156.2) * mm});
            skLineSegment(sketch, "E757", {"start": v(52.08, 156.2) * mm, "end": v(52.47, 156.08) * mm});
            skLineSegment(sketch, "E758", {"start": v(52.47, 156.08) * mm, "end": v(52.85, 155.94) * mm});
            skLineSegment(sketch, "E759", {"start": v(52.85, 155.94) * mm, "end": v(53.23, 155.8) * mm});
            skLineSegment(sketch, "E760", {"start": v(53.23, 155.8) * mm, "end": v(53.6, 155.64) * mm});
            skLineSegment(sketch, "E761", {"start": v(53.6, 155.64) * mm, "end": v(53.98, 155.47) * mm});
            skLineSegment(sketch, "E762", {"start": v(53.98, 155.47) * mm, "end": v(54.35, 155.3) * mm});
            skLineSegment(sketch, "E763", {"start": v(54.35, 155.3) * mm, "end": v(54.71, 155.11) * mm});
            skLineSegment(sketch, "E764", {"start": v(54.71, 155.11) * mm, "end": v(55.07, 154.92) * mm});
            skLineSegment(sketch, "E765", {"start": v(55.07, 154.92) * mm, "end": v(55.42, 154.71) * mm});
            skLineSegment(sketch, "E766", {"start": v(55.42, 154.71) * mm, "end": v(55.77, 154.5) * mm});
            skLineSegment(sketch, "E767", {"start": v(55.77, 154.5) * mm, "end": v(56.12, 154.28) * mm});
            skLineSegment(sketch, "E768", {"start": v(56.12, 154.28) * mm, "end": v(56.45, 154.05) * mm});
            skLineSegment(sketch, "E769", {"start": v(56.45, 154.05) * mm, "end": v(56.79, 153.81) * mm});
            skLineSegment(sketch, "E770", {"start": v(56.79, 153.81) * mm, "end": v(57.11, 153.56) * mm});
            skLineSegment(sketch, "E771", {"start": v(57.11, 153.56) * mm, "end": v(57.43, 153.3) * mm});
            skLineSegment(sketch, "E772", {"start": v(57.43, 153.3) * mm, "end": v(57.75, 153.04) * mm});
            skLineSegment(sketch, "E773", {"start": v(57.75, 153.04) * mm, "end": v(58.05, 152.77) * mm});
            skLineSegment(sketch, "E774", {"start": v(58.05, 152.77) * mm, "end": v(58.36, 152.48) * mm});
            skLineSegment(sketch, "E775", {"start": v(58.36, 152.48) * mm, "end": v(58.65, 152.2) * mm});
            skLineSegment(sketch, "E776", {"start": v(58.65, 152.2) * mm, "end": v(58.94, 151.9) * mm});
            skLineSegment(sketch, "E777", {"start": v(58.94, 151.9) * mm, "end": v(59.3, 151.48) * mm});
            skLineSegment(sketch, "E778", {"start": v(59.3, 151.48) * mm, "end": v(59.67, 151.07) * mm});
            skLineSegment(sketch, "E779", {"start": v(59.67, 151.07) * mm, "end": v(60.01, 150.64) * mm});
            skLineSegment(sketch, "E780", {"start": v(60.01, 150.64) * mm, "end": v(60.35, 150.2) * mm});
            skLineSegment(sketch, "E781", {"start": v(60.35, 150.2) * mm, "end": v(60.67, 149.77) * mm});
            skLineSegment(sketch, "E782", {"start": v(60.67, 149.77) * mm, "end": v(60.99, 149.32) * mm});
            skLineSegment(sketch, "E783", {"start": v(60.99, 149.32) * mm, "end": v(61.29, 148.86) * mm});
            skLineSegment(sketch, "E784", {"start": v(61.29, 148.86) * mm, "end": v(61.58, 148.4) * mm});
            skLineSegment(sketch, "E785", {"start": v(61.58, 148.4) * mm, "end": v(61.86, 147.93) * mm});
            skLineSegment(sketch, "E786", {"start": v(61.86, 147.93) * mm, "end": v(62.12, 147.45) * mm});
            skLineSegment(sketch, "E787", {"start": v(62.12, 147.45) * mm, "end": v(62.38, 146.97) * mm});
            skLineSegment(sketch, "E788", {"start": v(62.38, 146.97) * mm, "end": v(62.62, 146.48) * mm});
            skLineSegment(sketch, "E789", {"start": v(62.62, 146.48) * mm, "end": v(62.85, 145.99) * mm});
            skLineSegment(sketch, "E790", {"start": v(62.85, 145.99) * mm, "end": v(63.07, 145.49) * mm});
            skLineSegment(sketch, "E791", {"start": v(63.07, 145.49) * mm, "end": v(63.27, 144.99) * mm});
            skLineSegment(sketch, "E792", {"start": v(63.27, 144.99) * mm, "end": v(63.46, 144.48) * mm});
            skLineSegment(sketch, "E793", {"start": v(63.46, 144.48) * mm, "end": v(63.64, 143.96) * mm});
            skLineSegment(sketch, "E794", {"start": v(63.64, 143.96) * mm, "end": v(63.81, 143.45) * mm});
            skLineSegment(sketch, "E795", {"start": v(63.81, 143.45) * mm, "end": v(63.97, 142.92) * mm});
            skLineSegment(sketch, "E796", {"start": v(63.97, 142.92) * mm, "end": v(64.1, 142.4) * mm});
            skLineSegment(sketch, "E797", {"start": v(64.1, 142.4) * mm, "end": v(64.24, 141.87) * mm});
            skLineSegment(sketch, "E798", {"start": v(64.24, 141.87) * mm, "end": v(64.35, 141.34) * mm});
            skLineSegment(sketch, "E799", {"start": v(64.35, 141.34) * mm, "end": v(64.45, 140.8) * mm});
            skLineSegment(sketch, "E800", {"start": v(64.45, 140.8) * mm, "end": v(64.54, 140.26) * mm});
            skLineSegment(sketch, "E801", {"start": v(64.54, 140.26) * mm, "end": v(64.62, 139.72) * mm});
            skLineSegment(sketch, "E802", {"start": v(64.62, 139.72) * mm, "end": v(64.68, 139.18) * mm});
            skLineSegment(sketch, "E803", {"start": v(64.68, 139.18) * mm, "end": v(64.73, 138.63) * mm});
            skLineSegment(sketch, "E804", {"start": v(64.73, 138.63) * mm, "end": v(64.77, 138.09) * mm});
            skLineSegment(sketch, "E805", {"start": v(64.77, 138.09) * mm, "end": v(64.79, 137.54) * mm});
            skLineSegment(sketch, "E806", {"start": v(64.79, 137.54) * mm, "end": v(64.8, 136.99) * mm});
            skLineSegment(sketch, "E807", {"start": v(64.8, 136.99) * mm, "end": v(64.8, 136.44) * mm});
            skLineSegment(sketch, "E808", {"start": v(64.8, 136.44) * mm, "end": v(64.77, 135.89) * mm});
            skLineSegment(sketch, "E809", {"start": v(64.77, 135.89) * mm, "end": v(64.78, 135.37) * mm});
            skLineSegment(sketch, "E810", {"start": v(64.78, 135.37) * mm, "end": v(64.77, 134.86) * mm});
            skLineSegment(sketch, "E811", {"start": v(64.77, 134.86) * mm, "end": v(64.76, 134.35) * mm});
            skLineSegment(sketch, "E812", {"start": v(64.76, 134.35) * mm, "end": v(64.73, 133.83) * mm});
            skLineSegment(sketch, "E813", {"start": v(64.73, 133.83) * mm, "end": v(64.68, 133.32) * mm});
            skLineSegment(sketch, "E814", {"start": v(64.68, 133.32) * mm, "end": v(64.63, 132.82) * mm});
            skLineSegment(sketch, "E815", {"start": v(64.63, 132.82) * mm, "end": v(64.56, 132.31) * mm});
            skLineSegment(sketch, "E816", {"start": v(64.56, 132.31) * mm, "end": v(64.48, 131.8) * mm});
            skLineSegment(sketch, "E817", {"start": v(64.48, 131.8) * mm, "end": v(64.38, 131.3) * mm});
            skLineSegment(sketch, "E818", {"start": v(64.38, 131.3) * mm, "end": v(64.28, 130.81) * mm});
            skLineSegment(sketch, "E819", {"start": v(64.28, 130.81) * mm, "end": v(64.16, 130.32) * mm});
            skLineSegment(sketch, "E820", {"start": v(64.16, 130.32) * mm, "end": v(64.03, 129.83) * mm});
            skLineSegment(sketch, "E821", {"start": v(64.03, 129.83) * mm, "end": v(63.89, 129.34) * mm});
            skLineSegment(sketch, "E822", {"start": v(63.89, 129.34) * mm, "end": v(63.73, 128.86) * mm});
            skLineSegment(sketch, "E823", {"start": v(63.73, 128.86) * mm, "end": v(63.57, 128.38) * mm});
            skLineSegment(sketch, "E824", {"start": v(63.57, 128.38) * mm, "end": v(63.39, 127.9) * mm});
            skLineSegment(sketch, "E825", {"start": v(63.39, 127.9) * mm, "end": v(63.2, 127.43) * mm});
            skLineSegment(sketch, "E826", {"start": v(63.2, 127.43) * mm, "end": v(63, 126.97) * mm});
            skLineSegment(sketch, "E827", {"start": v(63, 126.97) * mm, "end": v(62.78, 126.5) * mm});
            skLineSegment(sketch, "E828", {"start": v(62.78, 126.5) * mm, "end": v(62.56, 126.05) * mm});
            skLineSegment(sketch, "E829", {"start": v(62.56, 126.05) * mm, "end": v(62.32, 125.6) * mm});
            skLineSegment(sketch, "E830", {"start": v(62.32, 125.6) * mm, "end": v(62.08, 125.16) * mm});
            skLineSegment(sketch, "E831", {"start": v(62.08, 125.16) * mm, "end": v(61.82, 124.72) * mm});
            skLineSegment(sketch, "E832", {"start": v(61.82, 124.72) * mm, "end": v(61.55, 124.29) * mm});
            skLineSegment(sketch, "E833", {"start": v(61.55, 124.29) * mm, "end": v(61.27, 123.86) * mm});
            skLineSegment(sketch, "E834", {"start": v(61.27, 123.86) * mm, "end": v(60.98, 123.44) * mm});
            skLineSegment(sketch, "E835", {"start": v(60.98, 123.44) * mm, "end": v(60.68, 123.03) * mm});
            skLineSegment(sketch, "E836", {"start": v(60.68, 123.03) * mm, "end": v(60.36, 122.63) * mm});
            skLineSegment(sketch, "E837", {"start": v(60.36, 122.63) * mm, "end": v(60.04, 122.23) * mm});
            skLineSegment(sketch, "E838", {"start": v(60.04, 122.23) * mm, "end": v(59.7, 121.84) * mm});
            skLineSegment(sketch, "E839", {"start": v(59.7, 121.84) * mm, "end": v(59.36, 121.46) * mm});
            skLineSegment(sketch, "E840", {"start": v(59.36, 121.46) * mm, "end": v(59, 121.08) * mm});
            skLineSegment(sketch, "E841", {"start": v(59, 121.08) * mm, "end": v(58.71, 120.8) * mm});
            skLineSegment(sketch, "E842", {"start": v(58.71, 120.8) * mm, "end": v(58.41, 120.5) * mm});
            skLineSegment(sketch, "E843", {"start": v(58.41, 120.5) * mm, "end": v(58.1, 120.23) * mm});
            skLineSegment(sketch, "E844", {"start": v(58.1, 120.23) * mm, "end": v(57.8, 119.97) * mm});
            skLineSegment(sketch, "E845", {"start": v(57.8, 119.97) * mm, "end": v(57.47, 119.7) * mm});
            skLineSegment(sketch, "E846", {"start": v(57.47, 119.7) * mm, "end": v(57.15, 119.46) * mm});
            skLineSegment(sketch, "E847", {"start": v(57.15, 119.46) * mm, "end": v(56.82, 119.22) * mm});
            skLineSegment(sketch, "E848", {"start": v(56.82, 119.22) * mm, "end": v(56.48, 118.99) * mm});
            skLineSegment(sketch, "E849", {"start": v(56.48, 118.99) * mm, "end": v(56.14, 118.76) * mm});
            skLineSegment(sketch, "E850", {"start": v(56.14, 118.76) * mm, "end": v(55.8, 118.55) * mm});
            skLineSegment(sketch, "E851", {"start": v(55.8, 118.55) * mm, "end": v(55.44, 118.34) * mm});
            skLineSegment(sketch, "E852", {"start": v(55.44, 118.34) * mm, "end": v(55.08, 118.14) * mm});
            skLineSegment(sketch, "E853", {"start": v(55.08, 118.14) * mm, "end": v(54.72, 117.95) * mm});
            skLineSegment(sketch, "E854", {"start": v(54.72, 117.95) * mm, "end": v(54.35, 117.77) * mm});
            skLineSegment(sketch, "E855", {"start": v(54.35, 117.77) * mm, "end": v(53.98, 117.6) * mm});
            skLineSegment(sketch, "E856", {"start": v(53.98, 117.6) * mm, "end": v(53.6, 117.44) * mm});
            skLineSegment(sketch, "E857", {"start": v(53.6, 117.44) * mm, "end": v(53.23, 117.3) * mm});
            skLineSegment(sketch, "E858", {"start": v(53.23, 117.3) * mm, "end": v(52.85, 117.15) * mm});
            skLineSegment(sketch, "E859", {"start": v(52.85, 117.15) * mm, "end": v(52.46, 117.02) * mm});
            skLineSegment(sketch, "E860", {"start": v(52.46, 117.02) * mm, "end": v(52.07, 116.9) * mm});
            skLineSegment(sketch, "E861", {"start": v(52.07, 116.9) * mm, "end": v(51.68, 116.78) * mm});
            skLineSegment(sketch, "E862", {"start": v(51.68, 116.78) * mm, "end": v(51.29, 116.68) * mm});
            skLineSegment(sketch, "E863", {"start": v(51.29, 116.68) * mm, "end": v(50.89, 116.58) * mm});
            skLineSegment(sketch, "E864", {"start": v(50.89, 116.58) * mm, "end": v(50.49, 116.5) * mm});
            skLineSegment(sketch, "E865", {"start": v(50.49, 116.5) * mm, "end": v(50.09, 116.42) * mm});
            skLineSegment(sketch, "E866", {"start": v(50.09, 116.42) * mm, "end": v(49.68, 116.36) * mm});
            skLineSegment(sketch, "E867", {"start": v(49.68, 116.36) * mm, "end": v(49.28, 116.3) * mm});
            skLineSegment(sketch, "E868", {"start": v(49.28, 116.3) * mm, "end": v(48.87, 116.26) * mm});
            skLineSegment(sketch, "E869", {"start": v(48.87, 116.26) * mm, "end": v(48.46, 116.22) * mm});
            skLineSegment(sketch, "E870", {"start": v(48.46, 116.22) * mm, "end": v(48.05, 116.2) * mm});
            skLineSegment(sketch, "E871", {"start": v(48.05, 116.2) * mm, "end": v(47.63, 116.19) * mm});
            skLineSegment(sketch, "E872", {"start": v(47.63, 116.19) * mm, "end": v(47.22, 116.19) * mm});
            skLineSegment(sketch, "E873", {"start": v(73.8, 116.72) * mm, "end": v(73.8, 156.71) * mm});
            skLineSegment(sketch, "E874", {"start": v(73.8, 156.71) * mm, "end": v(98.66, 156.71) * mm});
            skLineSegment(sketch, "E875", {"start": v(73.8, 137.6) * mm, "end": v(96.87, 137.6) * mm});
            skLineSegment(sketch, "E876", {"start": v(134.26, 146.67) * mm, "end": v(134.3, 147.23) * mm});
            skLineSegment(sketch, "E877", {"start": v(134.3, 147.23) * mm, "end": v(134.38, 147.79) * mm});
            skLineSegment(sketch, "E878", {"start": v(134.38, 147.79) * mm, "end": v(134.48, 148.34) * mm});
            skLineSegment(sketch, "E879", {"start": v(134.48, 148.34) * mm, "end": v(134.6, 148.88) * mm});
            skLineSegment(sketch, "E880", {"start": v(134.6, 148.88) * mm, "end": v(134.75, 149.4) * mm});
            skLineSegment(sketch, "E881", {"start": v(134.75, 149.4) * mm, "end": v(134.93, 149.93) * mm});
            skLineSegment(sketch, "E882", {"start": v(134.93, 149.93) * mm, "end": v(135.12, 150.43) * mm});
            skLineSegment(sketch, "E883", {"start": v(135.12, 150.43) * mm, "end": v(135.34, 150.93) * mm});
            skLineSegment(sketch, "E884", {"start": v(135.34, 150.93) * mm, "end": v(135.59, 151.41) * mm});
            skLineSegment(sketch, "E885", {"start": v(135.59, 151.41) * mm, "end": v(135.85, 151.88) * mm});
            skLineSegment(sketch, "E886", {"start": v(135.85, 151.88) * mm, "end": v(136.14, 152.34) * mm});
            skLineSegment(sketch, "E887", {"start": v(136.14, 152.34) * mm, "end": v(136.44, 152.78) * mm});
            skLineSegment(sketch, "E888", {"start": v(136.44, 152.78) * mm, "end": v(136.77, 153.2) * mm});
            skLineSegment(sketch, "E889", {"start": v(136.77, 153.2) * mm, "end": v(137.11, 153.62) * mm});
            skLineSegment(sketch, "E890", {"start": v(137.11, 153.62) * mm, "end": v(137.48, 154) * mm});
            skLineSegment(sketch, "E891", {"start": v(137.48, 154) * mm, "end": v(137.86, 154.39) * mm});
            skLineSegment(sketch, "E892", {"start": v(137.86, 154.39) * mm, "end": v(138.25, 154.74) * mm});
            skLineSegment(sketch, "E893", {"start": v(138.25, 154.74) * mm, "end": v(138.67, 155.08) * mm});
            skLineSegment(sketch, "E894", {"start": v(138.67, 155.08) * mm, "end": v(139.1, 155.4) * mm});
            skLineSegment(sketch, "E895", {"start": v(139.1, 155.4) * mm, "end": v(139.54, 155.7) * mm});
            skLineSegment(sketch, "E896", {"start": v(139.54, 155.7) * mm, "end": v(140, 155.99) * mm});
            skLineSegment(sketch, "E897", {"start": v(140, 155.99) * mm, "end": v(140.47, 156.25) * mm});
            skLineSegment(sketch, "E898", {"start": v(140.47, 156.25) * mm, "end": v(140.95, 156.48) * mm});
            skLineSegment(sketch, "E899", {"start": v(140.95, 156.48) * mm, "end": v(141.45, 156.7) * mm});
            skLineSegment(sketch, "E900", {"start": v(141.45, 156.7) * mm, "end": v(141.96, 156.9) * mm});
            skLineSegment(sketch, "E901", {"start": v(141.96, 156.9) * mm, "end": v(142.48, 157.06) * mm});
            skLineSegment(sketch, "E902", {"start": v(142.48, 157.06) * mm, "end": v(143, 157.2) * mm});
            skLineSegment(sketch, "E903", {"start": v(143, 157.2) * mm, "end": v(143.54, 157.33) * mm});
            skLineSegment(sketch, "E904", {"start": v(143.54, 157.33) * mm, "end": v(144.09, 157.42) * mm});
            skLineSegment(sketch, "E905", {"start": v(144.09, 157.42) * mm, "end": v(144.64, 157.49) * mm});
            skLineSegment(sketch, "E906", {"start": v(144.64, 157.49) * mm, "end": v(145.2, 157.53) * mm});
            skLineSegment(sketch, "E907", {"start": v(145.2, 157.53) * mm, "end": v(145.78, 157.55) * mm});
            skLineSegment(sketch, "E908", {"start": v(145.78, 157.55) * mm, "end": v(146.74, 157.55) * mm});
            skLineSegment(sketch, "E909", {"start": v(146.74, 157.55) * mm, "end": v(147.4, 157.53) * mm});
            skLineSegment(sketch, "E910", {"start": v(147.4, 157.53) * mm, "end": v(148.05, 157.5) * mm});
            skLineSegment(sketch, "E911", {"start": v(148.05, 157.5) * mm, "end": v(148.69, 157.43) * mm});
            skLineSegment(sketch, "E912", {"start": v(148.69, 157.43) * mm, "end": v(149.32, 157.34) * mm});
            skLineSegment(sketch, "E913", {"start": v(149.32, 157.34) * mm, "end": v(149.94, 157.23) * mm});
            skLineSegment(sketch, "E914", {"start": v(149.94, 157.23) * mm, "end": v(150.54, 157.1) * mm});
            skLineSegment(sketch, "E915", {"start": v(150.54, 157.1) * mm, "end": v(151.14, 156.94) * mm});
            skLineSegment(sketch, "E916", {"start": v(151.14, 156.94) * mm, "end": v(151.72, 156.77) * mm});
            skLineSegment(sketch, "E917", {"start": v(151.72, 156.77) * mm, "end": v(152.29, 156.57) * mm});
            skLineSegment(sketch, "E918", {"start": v(152.29, 156.57) * mm, "end": v(152.84, 156.35) * mm});
            skLineSegment(sketch, "E919", {"start": v(152.84, 156.35) * mm, "end": v(153.37, 156.1) * mm});
            skLineSegment(sketch, "E920", {"start": v(153.37, 156.1) * mm, "end": v(153.9, 155.85) * mm});
            skLineSegment(sketch, "E921", {"start": v(153.9, 155.85) * mm, "end": v(154.4, 155.57) * mm});
            skLineSegment(sketch, "E922", {"start": v(154.4, 155.57) * mm, "end": v(154.88, 155.28) * mm});
            skLineSegment(sketch, "E923", {"start": v(154.88, 155.28) * mm, "end": v(155.34, 154.97) * mm});
            skLineSegment(sketch, "E924", {"start": v(155.34, 154.97) * mm, "end": v(155.79, 154.64) * mm});
            skLineSegment(sketch, "E925", {"start": v(155.79, 154.64) * mm, "end": v(156.21, 154.3) * mm});
            skLineSegment(sketch, "E926", {"start": v(156.21, 154.3) * mm, "end": v(156.61, 153.94) * mm});
            skLineSegment(sketch, "E927", {"start": v(156.61, 153.94) * mm, "end": v(157, 153.56) * mm});
            skLineSegment(sketch, "E928", {"start": v(157, 153.56) * mm, "end": v(157.35, 153.17) * mm});
            skLineSegment(sketch, "E929", {"start": v(157.35, 153.17) * mm, "end": v(157.68, 152.77) * mm});
            skLineSegment(sketch, "E930", {"start": v(157.68, 152.77) * mm, "end": v(158, 152.35) * mm});
            skLineSegment(sketch, "E931", {"start": v(158, 152.35) * mm, "end": v(158.27, 151.93) * mm});
            skLineSegment(sketch, "E932", {"start": v(158.27, 151.93) * mm, "end": v(158.53, 151.49) * mm});
            skLineSegment(sketch, "E933", {"start": v(158.53, 151.49) * mm, "end": v(158.76, 151.04) * mm});
            skLineSegment(sketch, "E934", {"start": v(158.76, 151.04) * mm, "end": v(158.86, 150.8) * mm});
            skLineSegment(sketch, "E935", {"start": v(158.86, 150.8) * mm, "end": v(158.96, 150.57) * mm});
            skLineSegment(sketch, "E936", {"start": v(158.96, 150.57) * mm, "end": v(159.05, 150.34) * mm});
            skLineSegment(sketch, "E937", {"start": v(159.05, 150.34) * mm, "end": v(159.13, 150.1) * mm});
            skLineSegment(sketch, "E938", {"start": v(159.13, 150.1) * mm, "end": v(159.2, 149.87) * mm});
            skLineSegment(sketch, "E939", {"start": v(159.2, 149.87) * mm, "end": v(159.28, 149.62) * mm});
            skLineSegment(sketch, "E940", {"start": v(159.28, 149.62) * mm, "end": v(159.34, 149.38) * mm});
            skLineSegment(sketch, "E941", {"start": v(159.34, 149.38) * mm, "end": v(159.39, 149.14) * mm});
            skLineSegment(sketch, "E942", {"start": v(159.39, 149.14) * mm, "end": v(159.43, 148.89) * mm});
            skLineSegment(sketch, "E943", {"start": v(159.43, 148.89) * mm, "end": v(159.47, 148.64) * mm});
            skLineSegment(sketch, "E944", {"start": v(159.47, 148.64) * mm, "end": v(159.5, 148.39) * mm});
            skLineSegment(sketch, "E945", {"start": v(159.5, 148.39) * mm, "end": v(159.52, 148.14) * mm});
            skLineSegment(sketch, "E946", {"start": v(159.52, 148.14) * mm, "end": v(159.53, 147.88) * mm});
            skLineSegment(sketch, "E947", {"start": v(159.53, 147.88) * mm, "end": v(159.54, 147.63) * mm});
            skLineSegment(sketch, "E948", {"start": v(159.54, 147.63) * mm, "end": v(159.54, 147.15) * mm});
            skLineSegment(sketch, "E949", {"start": v(159.54, 147.15) * mm, "end": v(159.53, 146.85) * mm});
            skLineSegment(sketch, "E950", {"start": v(159.53, 146.85) * mm, "end": v(159.52, 146.56) * mm});
            skLineSegment(sketch, "E951", {"start": v(159.52, 146.56) * mm, "end": v(159.5, 146.26) * mm});
            skLineSegment(sketch, "E952", {"start": v(159.5, 146.26) * mm, "end": v(159.47, 145.97) * mm});
            skLineSegment(sketch, "E953", {"start": v(159.47, 145.97) * mm, "end": v(159.43, 145.68) * mm});
            skLineSegment(sketch, "E954", {"start": v(159.43, 145.68) * mm, "end": v(159.4, 145.4) * mm});
            skLineSegment(sketch, "E955", {"start": v(159.4, 145.4) * mm, "end": v(159.34, 145.1) * mm});
            skLineSegment(sketch, "E956", {"start": v(159.34, 145.1) * mm, "end": v(159.28, 144.82) * mm});
            skLineSegment(sketch, "E957", {"start": v(159.28, 144.82) * mm, "end": v(159.21, 144.54) * mm});
            skLineSegment(sketch, "E958", {"start": v(159.21, 144.54) * mm, "end": v(159.13, 144.26) * mm});
            skLineSegment(sketch, "E959", {"start": v(159.13, 144.26) * mm, "end": v(159.05, 143.98) * mm});
            skLineSegment(sketch, "E960", {"start": v(159.05, 143.98) * mm, "end": v(158.96, 143.7) * mm});
            skLineSegment(sketch, "E961", {"start": v(158.96, 143.7) * mm, "end": v(158.86, 143.44) * mm});
            skLineSegment(sketch, "E962", {"start": v(158.86, 143.44) * mm, "end": v(158.76, 143.17) * mm});
            skLineSegment(sketch, "E963", {"start": v(158.76, 143.17) * mm, "end": v(158.65, 142.9) * mm});
            skLineSegment(sketch, "E964", {"start": v(158.65, 142.9) * mm, "end": v(158.53, 142.64) * mm});
            skLineSegment(sketch, "E965", {"start": v(158.53, 142.64) * mm, "end": v(158.4, 142.37) * mm});
            skLineSegment(sketch, "E966", {"start": v(158.4, 142.37) * mm, "end": v(158.27, 142.12) * mm});
            skLineSegment(sketch, "E967", {"start": v(158.27, 142.12) * mm, "end": v(158.13, 141.87) * mm});
            skLineSegment(sketch, "E968", {"start": v(158.13, 141.87) * mm, "end": v(157.98, 141.62) * mm});
            skLineSegment(sketch, "E969", {"start": v(157.98, 141.62) * mm, "end": v(157.82, 141.37) * mm});
            skLineSegment(sketch, "E970", {"start": v(157.82, 141.37) * mm, "end": v(157.66, 141.13) * mm});
            skLineSegment(sketch, "E971", {"start": v(157.66, 141.13) * mm, "end": v(157.5, 140.9) * mm});
            skLineSegment(sketch, "E972", {"start": v(157.5, 140.9) * mm, "end": v(157.32, 140.66) * mm});
            skLineSegment(sketch, "E973", {"start": v(157.32, 140.66) * mm, "end": v(157.14, 140.43) * mm});
            skLineSegment(sketch, "E974", {"start": v(157.14, 140.43) * mm, "end": v(156.95, 140.21) * mm});
            skLineSegment(sketch, "E975", {"start": v(156.95, 140.21) * mm, "end": v(156.76, 140) * mm});
            skLineSegment(sketch, "E976", {"start": v(156.76, 140) * mm, "end": v(156.56, 139.78) * mm});
            skLineSegment(sketch, "E977", {"start": v(156.56, 139.78) * mm, "end": v(156.35, 139.57) * mm});
            skLineSegment(sketch, "E978", {"start": v(156.35, 139.57) * mm, "end": v(156.14, 139.37) * mm});
            skLineSegment(sketch, "E979", {"start": v(156.14, 139.37) * mm, "end": v(155.92, 139.18) * mm});
            skLineSegment(sketch, "E980", {"start": v(155.92, 139.18) * mm, "end": v(155.7, 138.99) * mm});
            skLineSegment(sketch, "E981", {"start": v(155.7, 138.99) * mm, "end": v(140.5, 129.07) * mm});
            skLineSegment(sketch, "E982", {"start": v(140.5, 129.07) * mm, "end": v(140.11, 128.8) * mm});
            skLineSegment(sketch, "E983", {"start": v(140.11, 128.8) * mm, "end": v(139.74, 128.53) * mm});
            skLineSegment(sketch, "E984", {"start": v(139.74, 128.53) * mm, "end": v(139.37, 128.25) * mm});
            skLineSegment(sketch, "E985", {"start": v(139.37, 128.25) * mm, "end": v(139.01, 127.96) * mm});
            skLineSegment(sketch, "E986", {"start": v(139.01, 127.96) * mm, "end": v(138.67, 127.66) * mm});
            skLineSegment(sketch, "E987", {"start": v(138.67, 127.66) * mm, "end": v(138.33, 127.34) * mm});
            skLineSegment(sketch, "E988", {"start": v(138.33, 127.34) * mm, "end": v(138, 127.02) * mm});
            skLineSegment(sketch, "E989", {"start": v(138, 127.02) * mm, "end": v(137.7, 126.7) * mm});
            skLineSegment(sketch, "E990", {"start": v(137.7, 126.7) * mm, "end": v(137.4, 126.35) * mm});
            skLineSegment(sketch, "E991", {"start": v(137.4, 126.35) * mm, "end": v(137.1, 126) * mm});
            skLineSegment(sketch, "E992", {"start": v(137.1, 126) * mm, "end": v(136.82, 125.64) * mm});
            skLineSegment(sketch, "E993", {"start": v(136.82, 125.64) * mm, "end": v(136.55, 125.28) * mm});
            skLineSegment(sketch, "E994", {"start": v(136.55, 125.28) * mm, "end": v(136.3, 124.9) * mm});
            skLineSegment(sketch, "E995", {"start": v(136.3, 124.9) * mm, "end": v(136.04, 124.53) * mm});
            skLineSegment(sketch, "E996", {"start": v(136.04, 124.53) * mm, "end": v(135.8, 124.14) * mm});
            skLineSegment(sketch, "E997", {"start": v(135.8, 124.14) * mm, "end": v(135.59, 123.75) * mm});
            skLineSegment(sketch, "E998", {"start": v(135.59, 123.75) * mm, "end": v(135.38, 123.34) * mm});
            skLineSegment(sketch, "E999", {"start": v(135.38, 123.34) * mm, "end": v(135.18, 122.94) * mm});
            skLineSegment(sketch, "E1000", {"start": v(135.18, 122.94) * mm, "end": v(135, 122.52) * mm});
            skLineSegment(sketch, "E1001", {"start": v(135, 122.52) * mm, "end": v(134.82, 122.1) * mm});
            skLineSegment(sketch, "E1002", {"start": v(134.82, 122.1) * mm, "end": v(134.66, 121.68) * mm});
            skLineSegment(sketch, "E1003", {"start": v(134.66, 121.68) * mm, "end": v(134.5, 121.25) * mm});
            skLineSegment(sketch, "E1004", {"start": v(134.5, 121.25) * mm, "end": v(134.37, 120.82) * mm});
            skLineSegment(sketch, "E1005", {"start": v(134.37, 120.82) * mm, "end": v(134.25, 120.38) * mm});
            skLineSegment(sketch, "E1006", {"start": v(134.25, 120.38) * mm, "end": v(134.14, 119.94) * mm});
            skLineSegment(sketch, "E1007", {"start": v(134.14, 119.94) * mm, "end": v(134.05, 119.5) * mm});
            skLineSegment(sketch, "E1008", {"start": v(134.05, 119.5) * mm, "end": v(133.97, 119.04) * mm});
            skLineSegment(sketch, "E1009", {"start": v(133.97, 119.04) * mm, "end": v(133.9, 118.59) * mm});
            skLineSegment(sketch, "E1010", {"start": v(133.9, 118.59) * mm, "end": v(133.85, 118.13) * mm});
            skLineSegment(sketch, "E1011", {"start": v(133.85, 118.13) * mm, "end": v(133.81, 117.67) * mm});
            skLineSegment(sketch, "E1012", {"start": v(133.81, 117.67) * mm, "end": v(133.79, 117.2) * mm});
            skLineSegment(sketch, "E1013", {"start": v(133.79, 117.2) * mm, "end": v(133.78, 116.75) * mm});
            skLineSegment(sketch, "E1014", {"start": v(133.78, 116.75) * mm, "end": v(160.34, 116.75) * mm});
            skArc(sketch, "E1015", {"start": v(-519.75, 981.97) * mm, "mid": v(-518.65, 984.63) * mm, "end": v(-516, 985.72) * mm});
            skArc(sketch, "E1016", {"start": v(-516, 985.72) * mm, "mid": v(-513.35, 984.63) * mm, "end": v(-512.25, 981.97) * mm});
            skArc(sketch, "E1017", {"start": v(-512.25, 981.97) * mm, "mid": v(-513.35, 979.32) * mm, "end": v(-516, 978.22) * mm});
            skArc(sketch, "E1018", {"start": v(-516, 978.22) * mm, "mid": v(-518.65, 979.32) * mm, "end": v(-519.75, 981.97) * mm});
            skArc(sketch, "E1019", {"start": v(-466.24, 981.97) * mm, "mid": v(-465.14, 984.63) * mm, "end": v(-462.5, 985.72) * mm});
            skArc(sketch, "E1020", {"start": v(-462.5, 985.72) * mm, "mid": v(-459.84, 984.63) * mm, "end": v(-458.74, 981.97) * mm});
            skArc(sketch, "E1021", {"start": v(-458.74, 981.97) * mm, "mid": v(-459.84, 979.32) * mm, "end": v(-462.5, 978.22) * mm});
            skArc(sketch, "E1022", {"start": v(-462.5, 978.22) * mm, "mid": v(-465.14, 979.32) * mm, "end": v(-466.24, 981.97) * mm});
            skArc(sketch, "E1023", {"start": v(-519.75, 831.97) * mm, "mid": v(-518.65, 834.63) * mm, "end": v(-516, 835.72) * mm});
            skArc(sketch, "E1024", {"start": v(-516, 835.72) * mm, "mid": v(-513.35, 834.63) * mm, "end": v(-512.25, 831.97) * mm});
            skArc(sketch, "E1025", {"start": v(-512.25, 831.97) * mm, "mid": v(-513.35, 829.32) * mm, "end": v(-516, 828.22) * mm});
            skArc(sketch, "E1026", {"start": v(-516, 828.22) * mm, "mid": v(-518.65, 829.32) * mm, "end": v(-519.75, 831.97) * mm});
            skArc(sketch, "E1027", {"start": v(-466.24, 831.97) * mm, "mid": v(-465.14, 834.63) * mm, "end": v(-462.5, 835.72) * mm});
            skArc(sketch, "E1028", {"start": v(-462.5, 835.72) * mm, "mid": v(-459.84, 834.63) * mm, "end": v(-458.74, 831.97) * mm});
            skArc(sketch, "E1029", {"start": v(-458.74, 831.97) * mm, "mid": v(-459.84, 829.32) * mm, "end": v(-462.5, 828.22) * mm});
            skArc(sketch, "E1030", {"start": v(-462.5, 828.22) * mm, "mid": v(-465.14, 829.32) * mm, "end": v(-466.24, 831.97) * mm});
            skArc(sketch, "E1031", {"start": v(-519.75, 681.97) * mm, "mid": v(-518.65, 684.63) * mm, "end": v(-516, 685.72) * mm});
            skArc(sketch, "E1032", {"start": v(-516, 685.72) * mm, "mid": v(-513.35, 684.63) * mm, "end": v(-512.25, 681.97) * mm});
            skArc(sketch, "E1033", {"start": v(-512.25, 681.97) * mm, "mid": v(-513.35, 679.32) * mm, "end": v(-516, 678.22) * mm});
            skArc(sketch, "E1034", {"start": v(-516, 678.22) * mm, "mid": v(-518.65, 679.32) * mm, "end": v(-519.75, 681.97) * mm});
            skArc(sketch, "E1035", {"start": v(-466.24, 681.97) * mm, "mid": v(-465.14, 684.63) * mm, "end": v(-462.5, 685.72) * mm});
            skArc(sketch, "E1036", {"start": v(-462.5, 685.72) * mm, "mid": v(-459.84, 684.63) * mm, "end": v(-458.74, 681.97) * mm});
            skArc(sketch, "E1037", {"start": v(-458.74, 681.97) * mm, "mid": v(-459.84, 679.32) * mm, "end": v(-462.5, 678.22) * mm});
            skArc(sketch, "E1038", {"start": v(-462.5, 678.22) * mm, "mid": v(-465.14, 679.32) * mm, "end": v(-466.24, 681.97) * mm});
            skArc(sketch, "E1039", {"start": v(-519.75, 531.97) * mm, "mid": v(-518.65, 534.63) * mm, "end": v(-516, 535.72) * mm});
            skArc(sketch, "E1040", {"start": v(-516, 535.72) * mm, "mid": v(-513.35, 534.63) * mm, "end": v(-512.25, 531.97) * mm});
            skArc(sketch, "E1041", {"start": v(-512.25, 531.97) * mm, "mid": v(-513.35, 529.32) * mm, "end": v(-516, 528.22) * mm});
            skArc(sketch, "E1042", {"start": v(-516, 528.22) * mm, "mid": v(-518.65, 529.32) * mm, "end": v(-519.75, 531.97) * mm});
            skArc(sketch, "E1043", {"start": v(-466.24, 531.97) * mm, "mid": v(-465.14, 534.63) * mm, "end": v(-462.5, 535.72) * mm});
            skArc(sketch, "E1044", {"start": v(-462.5, 535.72) * mm, "mid": v(-459.84, 534.63) * mm, "end": v(-458.74, 531.97) * mm});
            skArc(sketch, "E1045", {"start": v(-458.74, 531.97) * mm, "mid": v(-459.84, 529.32) * mm, "end": v(-462.5, 528.22) * mm});
            skArc(sketch, "E1046", {"start": v(-462.5, 528.22) * mm, "mid": v(-465.14, 529.32) * mm, "end": v(-466.24, 531.97) * mm});
            skArc(sketch, "E1047", {"start": v(-519.75, 381.97) * mm, "mid": v(-518.65, 384.63) * mm, "end": v(-516, 385.72) * mm});
            skArc(sketch, "E1048", {"start": v(-516, 385.72) * mm, "mid": v(-513.35, 384.63) * mm, "end": v(-512.25, 381.97) * mm});
            skArc(sketch, "E1049", {"start": v(-512.25, 381.97) * mm, "mid": v(-513.35, 379.32) * mm, "end": v(-516, 378.22) * mm});
            skArc(sketch, "E1050", {"start": v(-516, 378.22) * mm, "mid": v(-518.65, 379.32) * mm, "end": v(-519.75, 381.97) * mm});
            skArc(sketch, "E1051", {"start": v(-466.24, 381.97) * mm, "mid": v(-465.14, 384.63) * mm, "end": v(-462.5, 385.72) * mm});
            skArc(sketch, "E1052", {"start": v(-462.5, 385.72) * mm, "mid": v(-459.84, 384.63) * mm, "end": v(-458.74, 381.97) * mm});
            skArc(sketch, "E1053", {"start": v(-458.74, 381.97) * mm, "mid": v(-459.84, 379.32) * mm, "end": v(-462.5, 378.22) * mm});
            skArc(sketch, "E1054", {"start": v(-462.5, 378.22) * mm, "mid": v(-465.14, 379.32) * mm, "end": v(-466.24, 381.97) * mm});
            skArc(sketch, "E1055", {"start": v(-519.75, 231.97) * mm, "mid": v(-518.65, 234.63) * mm, "end": v(-516, 235.72) * mm});
            skArc(sketch, "E1056", {"start": v(-516, 235.72) * mm, "mid": v(-513.35, 234.63) * mm, "end": v(-512.25, 231.97) * mm});
            skArc(sketch, "E1057", {"start": v(-512.25, 231.97) * mm, "mid": v(-513.35, 229.32) * mm, "end": v(-516, 228.22) * mm});
            skArc(sketch, "E1058", {"start": v(-516, 228.22) * mm, "mid": v(-518.65, 229.32) * mm, "end": v(-519.75, 231.97) * mm});
            skArc(sketch, "E1059", {"start": v(-466.24, 231.97) * mm, "mid": v(-465.14, 234.63) * mm, "end": v(-462.5, 235.72) * mm});
            skArc(sketch, "E1060", {"start": v(-462.5, 235.72) * mm, "mid": v(-459.84, 234.63) * mm, "end": v(-458.74, 231.97) * mm});
            skArc(sketch, "E1061", {"start": v(-458.74, 231.97) * mm, "mid": v(-459.84, 229.32) * mm, "end": v(-462.5, 228.22) * mm});
            skArc(sketch, "E1062", {"start": v(-462.5, 228.22) * mm, "mid": v(-465.14, 229.32) * mm, "end": v(-466.24, 231.97) * mm});
            skArc(sketch, "E1063", {"start": v(-519.75, 111.97) * mm, "mid": v(-518.65, 114.63) * mm, "end": v(-516, 115.72) * mm});
            skArc(sketch, "E1064", {"start": v(-516, 115.72) * mm, "mid": v(-513.35, 114.63) * mm, "end": v(-512.25, 111.97) * mm});
            skArc(sketch, "E1065", {"start": v(-512.25, 111.97) * mm, "mid": v(-513.35, 109.32) * mm, "end": v(-516, 108.22) * mm});
            skArc(sketch, "E1066", {"start": v(-516, 108.22) * mm, "mid": v(-518.65, 109.32) * mm, "end": v(-519.75, 111.97) * mm});
            skArc(sketch, "E1067", {"start": v(-466.24, 111.97) * mm, "mid": v(-465.14, 114.63) * mm, "end": v(-462.5, 115.72) * mm});
            skArc(sketch, "E1068", {"start": v(-462.5, 115.72) * mm, "mid": v(-459.84, 114.63) * mm, "end": v(-458.74, 111.97) * mm});
            skArc(sketch, "E1069", {"start": v(-458.74, 111.97) * mm, "mid": v(-459.84, 109.32) * mm, "end": v(-462.5, 108.22) * mm});
            skArc(sketch, "E1070", {"start": v(-462.5, 108.22) * mm, "mid": v(-465.14, 109.32) * mm, "end": v(-466.24, 111.97) * mm});
            skArc(sketch, "E1071", {"start": v(-519.75, -68.03) * mm, "mid": v(-518.65, -65.37) * mm, "end": v(-516, -64.28) * mm});
            skArc(sketch, "E1072", {"start": v(-516, -64.28) * mm, "mid": v(-513.35, -65.37) * mm, "end": v(-512.25, -68.03) * mm});
            skArc(sketch, "E1073", {"start": v(-512.25, -68.03) * mm, "mid": v(-513.35, -70.68) * mm, "end": v(-516, -71.78) * mm});
            skArc(sketch, "E1074", {"start": v(-516, -71.78) * mm, "mid": v(-518.65, -70.68) * mm, "end": v(-519.75, -68.03) * mm});
            skArc(sketch, "E1075", {"start": v(-466.24, -68.03) * mm, "mid": v(-465.14, -65.37) * mm, "end": v(-462.5, -64.28) * mm});
            skArc(sketch, "E1076", {"start": v(-462.5, -64.28) * mm, "mid": v(-459.84, -65.37) * mm, "end": v(-458.74, -68.03) * mm});
            skArc(sketch, "E1077", {"start": v(-458.74, -68.03) * mm, "mid": v(-459.84, -70.68) * mm, "end": v(-462.5, -71.78) * mm});
            skArc(sketch, "E1078", {"start": v(-462.5, -71.78) * mm, "mid": v(-465.14, -70.68) * mm, "end": v(-466.24, -68.03) * mm});
            skArc(sketch, "E1079", {"start": v(-519.75, -218.03) * mm, "mid": v(-518.65, -215.37) * mm, "end": v(-516, -214.28) * mm});
            skArc(sketch, "E1080", {"start": v(-516, -214.28) * mm, "mid": v(-513.35, -215.37) * mm, "end": v(-512.25, -218.03) * mm});
            skArc(sketch, "E1081", {"start": v(-512.25, -218.03) * mm, "mid": v(-513.35, -220.68) * mm, "end": v(-516, -221.78) * mm});
            skArc(sketch, "E1082", {"start": v(-516, -221.78) * mm, "mid": v(-518.65, -220.68) * mm, "end": v(-519.75, -218.03) * mm});
            skArc(sketch, "E1083", {"start": v(-466.24, -218.03) * mm, "mid": v(-465.14, -215.37) * mm, "end": v(-462.5, -214.28) * mm});
            skArc(sketch, "E1084", {"start": v(-462.5, -214.28) * mm, "mid": v(-459.84, -215.37) * mm, "end": v(-458.74, -218.03) * mm});
            skArc(sketch, "E1085", {"start": v(-458.74, -218.03) * mm, "mid": v(-459.84, -220.68) * mm, "end": v(-462.5, -221.78) * mm});
            skArc(sketch, "E1086", {"start": v(-462.5, -221.78) * mm, "mid": v(-465.14, -220.68) * mm, "end": v(-466.24, -218.03) * mm});
            skArc(sketch, "E1087", {"start": v(-519.75, -368.03) * mm, "mid": v(-518.65, -365.37) * mm, "end": v(-516, -364.28) * mm});
            skArc(sketch, "E1088", {"start": v(-516, -364.28) * mm, "mid": v(-513.35, -365.37) * mm, "end": v(-512.25, -368.03) * mm});
            skArc(sketch, "E1089", {"start": v(-512.25, -368.03) * mm, "mid": v(-513.35, -370.68) * mm, "end": v(-516, -371.78) * mm});
            skArc(sketch, "E1090", {"start": v(-516, -371.78) * mm, "mid": v(-518.65, -370.68) * mm, "end": v(-519.75, -368.03) * mm});
            skArc(sketch, "E1091", {"start": v(-466.24, -368.03) * mm, "mid": v(-465.14, -365.37) * mm, "end": v(-462.5, -364.28) * mm});
            skArc(sketch, "E1092", {"start": v(-462.5, -364.28) * mm, "mid": v(-459.84, -365.37) * mm, "end": v(-458.74, -368.03) * mm});
            skArc(sketch, "E1093", {"start": v(-458.74, -368.03) * mm, "mid": v(-459.84, -370.68) * mm, "end": v(-462.5, -371.78) * mm});
            skArc(sketch, "E1094", {"start": v(-462.5, -371.78) * mm, "mid": v(-465.14, -370.68) * mm, "end": v(-466.24, -368.03) * mm});
            skArc(sketch, "E1095", {"start": v(-519.75, -518.03) * mm, "mid": v(-518.65, -515.37) * mm, "end": v(-516, -514.28) * mm});
            skArc(sketch, "E1096", {"start": v(-516, -514.28) * mm, "mid": v(-513.35, -515.37) * mm, "end": v(-512.25, -518.03) * mm});
            skArc(sketch, "E1097", {"start": v(-512.25, -518.03) * mm, "mid": v(-513.35, -520.68) * mm, "end": v(-516, -521.78) * mm});
            skArc(sketch, "E1098", {"start": v(-516, -521.78) * mm, "mid": v(-518.65, -520.68) * mm, "end": v(-519.75, -518.03) * mm});
            skArc(sketch, "E1099", {"start": v(-466.24, -518.03) * mm, "mid": v(-465.14, -515.37) * mm, "end": v(-462.5, -514.28) * mm});
            skArc(sketch, "E1100", {"start": v(-462.5, -514.28) * mm, "mid": v(-459.84, -515.37) * mm, "end": v(-458.74, -518.03) * mm});
            skArc(sketch, "E1101", {"start": v(-458.74, -518.03) * mm, "mid": v(-459.84, -520.68) * mm, "end": v(-462.5, -521.78) * mm});
            skArc(sketch, "E1102", {"start": v(-462.5, -521.78) * mm, "mid": v(-465.14, -520.68) * mm, "end": v(-466.24, -518.03) * mm});
            skArc(sketch, "E1103", {"start": v(-519.75, -668.03) * mm, "mid": v(-518.65, -665.37) * mm, "end": v(-516, -664.28) * mm});
            skArc(sketch, "E1104", {"start": v(-516, -664.28) * mm, "mid": v(-513.35, -665.37) * mm, "end": v(-512.25, -668.03) * mm});
            skArc(sketch, "E1105", {"start": v(-512.25, -668.03) * mm, "mid": v(-513.35, -670.68) * mm, "end": v(-516, -671.78) * mm});
            skArc(sketch, "E1106", {"start": v(-516, -671.78) * mm, "mid": v(-518.65, -670.68) * mm, "end": v(-519.75, -668.03) * mm});
            skArc(sketch, "E1107", {"start": v(-466.24, -668.03) * mm, "mid": v(-465.14, -665.37) * mm, "end": v(-462.5, -664.28) * mm});
            skArc(sketch, "E1108", {"start": v(-462.5, -664.28) * mm, "mid": v(-459.84, -665.37) * mm, "end": v(-458.74, -668.03) * mm});
            skArc(sketch, "E1109", {"start": v(-458.74, -668.03) * mm, "mid": v(-459.84, -670.68) * mm, "end": v(-462.5, -671.78) * mm});
            skArc(sketch, "E1110", {"start": v(-462.5, -671.78) * mm, "mid": v(-465.14, -670.68) * mm, "end": v(-466.24, -668.03) * mm});
            skArc(sketch, "E1111", {"start": v(-519.75, -818.03) * mm, "mid": v(-518.65, -815.37) * mm, "end": v(-516, -814.28) * mm});
            skArc(sketch, "E1112", {"start": v(-516, -814.28) * mm, "mid": v(-513.35, -815.37) * mm, "end": v(-512.25, -818.03) * mm});
            skArc(sketch, "E1113", {"start": v(-512.25, -818.03) * mm, "mid": v(-513.35, -820.68) * mm, "end": v(-516, -821.78) * mm});
            skArc(sketch, "E1114", {"start": v(-516, -821.78) * mm, "mid": v(-518.65, -820.68) * mm, "end": v(-519.75, -818.03) * mm});
            skArc(sketch, "E1115", {"start": v(-466.24, -818.03) * mm, "mid": v(-465.14, -815.37) * mm, "end": v(-462.5, -814.28) * mm});
            skArc(sketch, "E1116", {"start": v(-462.5, -814.28) * mm, "mid": v(-459.84, -815.37) * mm, "end": v(-458.74, -818.03) * mm});
            skArc(sketch, "E1117", {"start": v(-458.74, -818.03) * mm, "mid": v(-459.84, -820.68) * mm, "end": v(-462.5, -821.78) * mm});
            skArc(sketch, "E1118", {"start": v(-462.5, -821.78) * mm, "mid": v(-465.14, -820.68) * mm, "end": v(-466.24, -818.03) * mm});
            skArc(sketch, "E1119", {"start": v(-519.75, -968.03) * mm, "mid": v(-518.65, -965.37) * mm, "end": v(-516, -964.28) * mm});
            skArc(sketch, "E1120", {"start": v(-516, -964.28) * mm, "mid": v(-513.35, -965.37) * mm, "end": v(-512.25, -968.03) * mm});
            skArc(sketch, "E1121", {"start": v(-512.25, -968.03) * mm, "mid": v(-513.35, -970.68) * mm, "end": v(-516, -971.78) * mm});
            skArc(sketch, "E1122", {"start": v(-516, -971.78) * mm, "mid": v(-518.65, -970.68) * mm, "end": v(-519.75, -968.03) * mm});
            skArc(sketch, "E1123", {"start": v(-466.24, -968.03) * mm, "mid": v(-465.14, -965.37) * mm, "end": v(-462.5, -964.28) * mm});
            skArc(sketch, "E1124", {"start": v(-462.5, -964.28) * mm, "mid": v(-459.84, -965.37) * mm, "end": v(-458.74, -968.03) * mm});
            skArc(sketch, "E1125", {"start": v(-458.74, -968.03) * mm, "mid": v(-459.84, -970.68) * mm, "end": v(-462.5, -971.78) * mm});
            skArc(sketch, "E1126", {"start": v(-462.5, -971.78) * mm, "mid": v(-465.14, -970.68) * mm, "end": v(-466.24, -968.03) * mm});
            skArc(sketch, "E1127", {"start": v(-519.75, -1118.03) * mm, "mid": v(-518.65, -1115.37) * mm, "end": v(-516, -1114.28) * mm});
            skArc(sketch, "E1128", {"start": v(-516, -1114.28) * mm, "mid": v(-513.35, -1115.37) * mm, "end": v(-512.25, -1118.03) * mm});
            skArc(sketch, "E1129", {"start": v(-512.25, -1118.03) * mm, "mid": v(-513.35, -1120.68) * mm, "end": v(-516, -1121.78) * mm});
            skArc(sketch, "E1130", {"start": v(-516, -1121.78) * mm, "mid": v(-518.65, -1120.68) * mm, "end": v(-519.75, -1118.03) * mm});
            skArc(sketch, "E1131", {"start": v(-466.24, -1118.03) * mm, "mid": v(-465.14, -1115.37) * mm, "end": v(-462.5, -1114.28) * mm});
            skArc(sketch, "E1132", {"start": v(-462.5, -1114.28) * mm, "mid": v(-459.84, -1115.37) * mm, "end": v(-458.74, -1118.03) * mm});
            skArc(sketch, "E1133", {"start": v(-458.74, -1118.03) * mm, "mid": v(-459.84, -1120.68) * mm, "end": v(-462.5, -1121.78) * mm});
            skArc(sketch, "E1134", {"start": v(-462.5, -1121.78) * mm, "mid": v(-465.14, -1120.68) * mm, "end": v(-466.24, -1118.03) * mm});
            skArc(sketch, "E1135", {"start": v(-519.75, 51.97) * mm, "mid": v(-518.65, 54.63) * mm, "end": v(-516, 55.72) * mm});
            skArc(sketch, "E1136", {"start": v(-516, 55.72) * mm, "mid": v(-513.35, 54.63) * mm, "end": v(-512.25, 51.97) * mm});
            skArc(sketch, "E1137", {"start": v(-512.25, 51.97) * mm, "mid": v(-513.35, 49.32) * mm, "end": v(-516, 48.22) * mm});
            skArc(sketch, "E1138", {"start": v(-516, 48.22) * mm, "mid": v(-518.65, 49.32) * mm, "end": v(-519.75, 51.97) * mm});
            skArc(sketch, "E1139", {"start": v(-466.24, 51.97) * mm, "mid": v(-465.14, 54.63) * mm, "end": v(-462.5, 55.72) * mm});
            skArc(sketch, "E1140", {"start": v(-462.5, 55.72) * mm, "mid": v(-459.84, 54.63) * mm, "end": v(-458.74, 51.97) * mm});
            skArc(sketch, "E1141", {"start": v(-458.74, 51.97) * mm, "mid": v(-459.84, 49.32) * mm, "end": v(-462.5, 48.22) * mm});
            skArc(sketch, "E1142", {"start": v(-462.5, 48.22) * mm, "mid": v(-465.14, 49.32) * mm, "end": v(-466.24, 51.97) * mm});
            skArc(sketch, "E1143", {"start": v(569.14, 981.97) * mm, "mid": v(570.23, 984.63) * mm, "end": v(572.89, 985.72) * mm});
            skArc(sketch, "E1144", {"start": v(572.89, 985.72) * mm, "mid": v(575.54, 984.63) * mm, "end": v(576.64, 981.97) * mm});
            skArc(sketch, "E1145", {"start": v(576.64, 981.97) * mm, "mid": v(575.54, 979.32) * mm, "end": v(572.89, 978.22) * mm});
            skArc(sketch, "E1146", {"start": v(572.89, 978.22) * mm, "mid": v(570.23, 979.32) * mm, "end": v(569.14, 981.97) * mm});
            skArc(sketch, "E1147", {"start": v(569.14, 831.97) * mm, "mid": v(570.23, 834.63) * mm, "end": v(572.89, 835.72) * mm});
            skArc(sketch, "E1148", {"start": v(572.89, 835.72) * mm, "mid": v(575.54, 834.63) * mm, "end": v(576.64, 831.97) * mm});
            skArc(sketch, "E1149", {"start": v(576.64, 831.97) * mm, "mid": v(575.54, 829.32) * mm, "end": v(572.89, 828.22) * mm});
            skArc(sketch, "E1150", {"start": v(572.89, 828.22) * mm, "mid": v(570.23, 829.32) * mm, "end": v(569.14, 831.97) * mm});
            skArc(sketch, "E1151", {"start": v(569.14, 681.97) * mm, "mid": v(570.23, 684.63) * mm, "end": v(572.89, 685.72) * mm});
            skArc(sketch, "E1152", {"start": v(572.89, 685.72) * mm, "mid": v(575.54, 684.63) * mm, "end": v(576.64, 681.97) * mm});
            skArc(sketch, "E1153", {"start": v(576.64, 681.97) * mm, "mid": v(575.54, 679.32) * mm, "end": v(572.89, 678.22) * mm});
            skArc(sketch, "E1154", {"start": v(572.89, 678.22) * mm, "mid": v(570.23, 679.32) * mm, "end": v(569.14, 681.97) * mm});
            skArc(sketch, "E1155", {"start": v(569.14, 531.97) * mm, "mid": v(570.23, 534.63) * mm, "end": v(572.89, 535.72) * mm});
            skArc(sketch, "E1156", {"start": v(572.89, 535.72) * mm, "mid": v(575.54, 534.63) * mm, "end": v(576.64, 531.97) * mm});
            skArc(sketch, "E1157", {"start": v(576.64, 531.97) * mm, "mid": v(575.54, 529.32) * mm, "end": v(572.89, 528.22) * mm});
            skArc(sketch, "E1158", {"start": v(572.89, 528.22) * mm, "mid": v(570.23, 529.32) * mm, "end": v(569.14, 531.97) * mm});
            skArc(sketch, "E1159", {"start": v(569.14, 381.97) * mm, "mid": v(570.23, 384.63) * mm, "end": v(572.89, 385.72) * mm});
            skArc(sketch, "E1160", {"start": v(572.89, 385.72) * mm, "mid": v(575.54, 384.63) * mm, "end": v(576.64, 381.97) * mm});
            skArc(sketch, "E1161", {"start": v(576.64, 381.97) * mm, "mid": v(575.54, 379.32) * mm, "end": v(572.89, 378.22) * mm});
            skArc(sketch, "E1162", {"start": v(572.89, 378.22) * mm, "mid": v(570.23, 379.32) * mm, "end": v(569.14, 381.97) * mm});
            skArc(sketch, "E1163", {"start": v(569.14, 231.97) * mm, "mid": v(570.23, 234.63) * mm, "end": v(572.89, 235.72) * mm});
            skArc(sketch, "E1164", {"start": v(572.89, 235.72) * mm, "mid": v(575.54, 234.63) * mm, "end": v(576.64, 231.97) * mm});
            skArc(sketch, "E1165", {"start": v(576.64, 231.97) * mm, "mid": v(575.54, 229.32) * mm, "end": v(572.89, 228.22) * mm});
            skArc(sketch, "E1166", {"start": v(572.89, 228.22) * mm, "mid": v(570.23, 229.32) * mm, "end": v(569.14, 231.97) * mm});
            skArc(sketch, "E1167", {"start": v(569.14, 111.97) * mm, "mid": v(570.23, 114.63) * mm, "end": v(572.89, 115.72) * mm});
            skArc(sketch, "E1168", {"start": v(572.89, 115.72) * mm, "mid": v(575.54, 114.63) * mm, "end": v(576.64, 111.97) * mm});
            skArc(sketch, "E1169", {"start": v(576.64, 111.97) * mm, "mid": v(575.54, 109.32) * mm, "end": v(572.89, 108.22) * mm});
            skArc(sketch, "E1170", {"start": v(572.89, 108.22) * mm, "mid": v(570.23, 109.32) * mm, "end": v(569.14, 111.97) * mm});
            skArc(sketch, "E1171", {"start": v(569.14, -68.03) * mm, "mid": v(570.23, -65.37) * mm, "end": v(572.89, -64.28) * mm});
            skArc(sketch, "E1172", {"start": v(572.89, -64.28) * mm, "mid": v(575.54, -65.37) * mm, "end": v(576.64, -68.03) * mm});
            skArc(sketch, "E1173", {"start": v(576.64, -68.03) * mm, "mid": v(575.54, -70.68) * mm, "end": v(572.89, -71.78) * mm});
            skArc(sketch, "E1174", {"start": v(572.89, -71.78) * mm, "mid": v(570.23, -70.68) * mm, "end": v(569.14, -68.03) * mm});
            skArc(sketch, "E1175", {"start": v(569.14, -218.03) * mm, "mid": v(570.23, -215.37) * mm, "end": v(572.89, -214.28) * mm});
            skArc(sketch, "E1176", {"start": v(572.89, -214.28) * mm, "mid": v(575.54, -215.37) * mm, "end": v(576.64, -218.03) * mm});
            skArc(sketch, "E1177", {"start": v(576.64, -218.03) * mm, "mid": v(575.54, -220.68) * mm, "end": v(572.89, -221.78) * mm});
            skArc(sketch, "E1178", {"start": v(572.89, -221.78) * mm, "mid": v(570.23, -220.68) * mm, "end": v(569.14, -218.03) * mm});
            skArc(sketch, "E1179", {"start": v(569.14, -368.03) * mm, "mid": v(570.23, -365.37) * mm, "end": v(572.89, -364.28) * mm});
            skArc(sketch, "E1180", {"start": v(572.89, -364.28) * mm, "mid": v(575.54, -365.37) * mm, "end": v(576.64, -368.03) * mm});
            skArc(sketch, "E1181", {"start": v(576.64, -368.03) * mm, "mid": v(575.54, -370.68) * mm, "end": v(572.89, -371.78) * mm});
            skArc(sketch, "E1182", {"start": v(572.89, -371.78) * mm, "mid": v(570.23, -370.68) * mm, "end": v(569.14, -368.03) * mm});
            skArc(sketch, "E1183", {"start": v(569.14, -518.03) * mm, "mid": v(570.23, -515.37) * mm, "end": v(572.89, -514.28) * mm});
            skArc(sketch, "E1184", {"start": v(572.89, -514.28) * mm, "mid": v(575.54, -515.37) * mm, "end": v(576.64, -518.03) * mm});
            skArc(sketch, "E1185", {"start": v(576.64, -518.03) * mm, "mid": v(575.54, -520.68) * mm, "end": v(572.89, -521.78) * mm});
            skArc(sketch, "E1186", {"start": v(572.89, -521.78) * mm, "mid": v(570.23, -520.68) * mm, "end": v(569.14, -518.03) * mm});
            skArc(sketch, "E1187", {"start": v(569.14, -668.03) * mm, "mid": v(570.23, -665.37) * mm, "end": v(572.89, -664.28) * mm});
            skArc(sketch, "E1188", {"start": v(572.89, -664.28) * mm, "mid": v(575.54, -665.37) * mm, "end": v(576.64, -668.03) * mm});
            skArc(sketch, "E1189", {"start": v(576.64, -668.03) * mm, "mid": v(575.54, -670.68) * mm, "end": v(572.89, -671.78) * mm});
            skArc(sketch, "E1190", {"start": v(572.89, -671.78) * mm, "mid": v(570.23, -670.68) * mm, "end": v(569.14, -668.03) * mm});
            skArc(sketch, "E1191", {"start": v(569.14, -818.03) * mm, "mid": v(570.23, -815.37) * mm, "end": v(572.89, -814.28) * mm});
            skArc(sketch, "E1192", {"start": v(572.89, -814.28) * mm, "mid": v(575.54, -815.37) * mm, "end": v(576.64, -818.03) * mm});
            skArc(sketch, "E1193", {"start": v(576.64, -818.03) * mm, "mid": v(575.54, -820.68) * mm, "end": v(572.89, -821.78) * mm});
            skArc(sketch, "E1194", {"start": v(572.89, -821.78) * mm, "mid": v(570.23, -820.68) * mm, "end": v(569.14, -818.03) * mm});
            skArc(sketch, "E1195", {"start": v(569.14, -968.03) * mm, "mid": v(570.23, -965.37) * mm, "end": v(572.89, -964.28) * mm});
            skArc(sketch, "E1196", {"start": v(572.89, -964.28) * mm, "mid": v(575.54, -965.37) * mm, "end": v(576.64, -968.03) * mm});
            skArc(sketch, "E1197", {"start": v(576.64, -968.03) * mm, "mid": v(575.54, -970.68) * mm, "end": v(572.89, -971.78) * mm});
            skArc(sketch, "E1198", {"start": v(572.89, -971.78) * mm, "mid": v(570.23, -970.68) * mm, "end": v(569.14, -968.03) * mm});
            skArc(sketch, "E1199", {"start": v(569.14, -1118.03) * mm, "mid": v(570.23, -1115.37) * mm, "end": v(572.89, -1114.28) * mm});
            skArc(sketch, "E1200", {"start": v(572.89, -1114.28) * mm, "mid": v(575.54, -1115.37) * mm, "end": v(576.64, -1118.03) * mm});
            skArc(sketch, "E1201", {"start": v(576.64, -1118.03) * mm, "mid": v(575.54, -1120.68) * mm, "end": v(572.89, -1121.78) * mm});
            skArc(sketch, "E1202", {"start": v(572.89, -1121.78) * mm, "mid": v(570.23, -1120.68) * mm, "end": v(569.14, -1118.03) * mm});
            skArc(sketch, "E1203", {"start": v(569.14, 51.97) * mm, "mid": v(570.23, 54.63) * mm, "end": v(572.89, 55.72) * mm});
            skArc(sketch, "E1204", {"start": v(572.89, 55.72) * mm, "mid": v(575.54, 54.63) * mm, "end": v(576.64, 51.97) * mm});
            skArc(sketch, "E1205", {"start": v(576.64, 51.97) * mm, "mid": v(575.54, 49.32) * mm, "end": v(572.89, 48.22) * mm});
            skArc(sketch, "E1206", {"start": v(572.89, 48.22) * mm, "mid": v(570.23, 49.32) * mm, "end": v(569.14, 51.97) * mm});
            skArc(sketch, "E1207", {"start": v(48.2, -1087.17) * mm, "mid": v(45.54, -1088.27) * mm, "end": v(44.45, -1090.92) * mm});
            skArc(sketch, "E1208", {"start": v(44.45, -1090.92) * mm, "mid": v(45.54, -1093.57) * mm, "end": v(48.2, -1094.67) * mm});
            skArc(sketch, "E1209", {"start": v(48.2, -1094.67) * mm, "mid": v(50.85, -1093.57) * mm, "end": v(51.95, -1090.92) * mm});
            skArc(sketch, "E1210", {"start": v(51.95, -1090.92) * mm, "mid": v(50.85, -1088.27) * mm, "end": v(48.2, -1087.17) * mm});
            skArc(sketch, "E1211", {"start": v(36.46, -694.02) * mm, "mid": v(33.8, -695.11) * mm, "end": v(32.71, -697.77) * mm});
            skArc(sketch, "E1212", {"start": v(32.71, -697.77) * mm, "mid": v(33.8, -700.42) * mm, "end": v(36.46, -701.52) * mm});
            skArc(sketch, "E1213", {"start": v(36.46, -701.52) * mm, "mid": v(39.11, -700.42) * mm, "end": v(40.21, -697.77) * mm});
            skArc(sketch, "E1214", {"start": v(40.21, -697.77) * mm, "mid": v(39.11, -695.11) * mm, "end": v(36.46, -694.02) * mm});
            skArc(sketch, "E1215", {"start": v(42.33, -30.23) * mm, "mid": v(39.68, -31.33) * mm, "end": v(38.58, -33.98) * mm});
            skArc(sketch, "E1216", {"start": v(38.58, -33.98) * mm, "mid": v(39.68, -36.64) * mm, "end": v(42.33, -37.73) * mm});
            skArc(sketch, "E1217", {"start": v(42.33, -37.73) * mm, "mid": v(44.98, -36.64) * mm, "end": v(46.08, -33.98) * mm});
            skArc(sketch, "E1218", {"start": v(46.08, -33.98) * mm, "mid": v(44.98, -31.33) * mm, "end": v(42.33, -30.23) * mm});
            skArc(sketch, "E1219", {"start": v(36.46, 508.91) * mm, "mid": v(33.8, 507.81) * mm, "end": v(32.71, 505.16) * mm});
            skArc(sketch, "E1220", {"start": v(32.71, 505.16) * mm, "mid": v(33.8, 502.5) * mm, "end": v(36.46, 501.41) * mm});
            skArc(sketch, "E1221", {"start": v(36.46, 501.41) * mm, "mid": v(39.11, 502.5) * mm, "end": v(40.21, 505.16) * mm});
            skArc(sketch, "E1222", {"start": v(40.21, 505.16) * mm, "mid": v(39.11, 507.81) * mm, "end": v(36.46, 508.91) * mm});
            skArc(sketch, "E1223", {"start": v(42.33, 943.14) * mm, "mid": v(39.68, 942.04) * mm, "end": v(38.58, 939.39) * mm});
            skArc(sketch, "E1224", {"start": v(38.58, 939.39) * mm, "mid": v(39.68, 936.74) * mm, "end": v(42.33, 935.64) * mm});
            skArc(sketch, "E1225", {"start": v(42.33, 935.64) * mm, "mid": v(44.98, 936.74) * mm, "end": v(46.08, 939.39) * mm});
            skArc(sketch, "E1226", {"start": v(46.08, 939.39) * mm, "mid": v(44.98, 942.04) * mm, "end": v(42.33, 943.14) * mm});
            skArc(sketch, "E1227", {"start": v(-456.45, 1142.65) * mm, "mid": v(-459.1, 1141.55) * mm, "end": v(-460.2, 1138.9) * mm});
            skArc(sketch, "E1228", {"start": v(-460.2, 1138.9) * mm, "mid": v(-459.1, 1136.25) * mm, "end": v(-456.45, 1135.15) * mm});
            skArc(sketch, "E1229", {"start": v(-456.45, 1135.15) * mm, "mid": v(-453.8, 1136.25) * mm, "end": v(-452.7, 1138.9) * mm});
            skArc(sketch, "E1230", {"start": v(-452.7, 1138.9) * mm, "mid": v(-453.8, 1141.55) * mm, "end": v(-456.45, 1142.65) * mm});
            skArc(sketch, "E1231", {"start": v(12.99, 1136.78) * mm, "mid": v(10.34, 1135.68) * mm, "end": v(9.24, 1133.03) * mm});
            skArc(sketch, "E1232", {"start": v(9.24, 1133.03) * mm, "mid": v(10.34, 1130.38) * mm, "end": v(12.99, 1129.28) * mm});
            skArc(sketch, "E1233", {"start": v(12.99, 1129.28) * mm, "mid": v(15.64, 1130.38) * mm, "end": v(16.74, 1133.03) * mm});
            skArc(sketch, "E1234", {"start": v(16.74, 1133.03) * mm, "mid": v(15.64, 1135.68) * mm, "end": v(12.99, 1136.78) * mm});
            skArc(sketch, "E1235", {"start": v(488.3, 1130.91) * mm, "mid": v(485.64, 1129.82) * mm, "end": v(484.54, 1127.16) * mm});
            skArc(sketch, "E1236", {"start": v(484.54, 1127.16) * mm, "mid": v(485.64, 1124.51) * mm, "end": v(488.3, 1123.41) * mm});
            skArc(sketch, "E1237", {"start": v(488.3, 1123.41) * mm, "mid": v(490.94, 1124.51) * mm, "end": v(492.04, 1127.16) * mm});
            skArc(sketch, "E1238", {"start": v(492.04, 1127.16) * mm, "mid": v(490.94, 1129.82) * mm, "end": v(488.3, 1130.91) * mm});
            skSolve(sketch);
        }
        {
            var Q0;
            Q0 = qSketchRegion(id + "F0", true);
            var Q1;
            {var subQ0=sQuery(id+"F0.wireOp",EDGE,"E247");Q1=makeQuery(id+"F0.imprint","IMPRINT",FACE,{"disambiguationData":[TD([[makeQuery(id+"F0.imprint","IMPRINT",EDGE,{"derivedFrom":subQ0}),-1.0]])]});}
            var Q2;
            Q2=makeQuery(id+"F0.imprint","IMPRINT",FACE,{"disambiguationData":[TD([[makeQuery(id+"F0.imprint","IMPRINT",EDGE,{"derivedFrom":sQuery(id+"F0.wireOp",EDGE,"E361")}),-1.0]])]});
            var Q3;
            Q3=makeQuery(id+"F0.imprint","IMPRINT",FACE,{"disambiguationData":[TD([[makeQuery(id+"F0.imprint","IMPRINT",EDGE,{"derivedFrom":sQuery(id+"F0.wireOp",EDGE,"E617")}),-1.0]])]});
            extrude(context, id + "F1", {"entities" : qUnion([Q0, Q1, Q2, Q3]), "depth" : 18 * mm});
        }
    });
